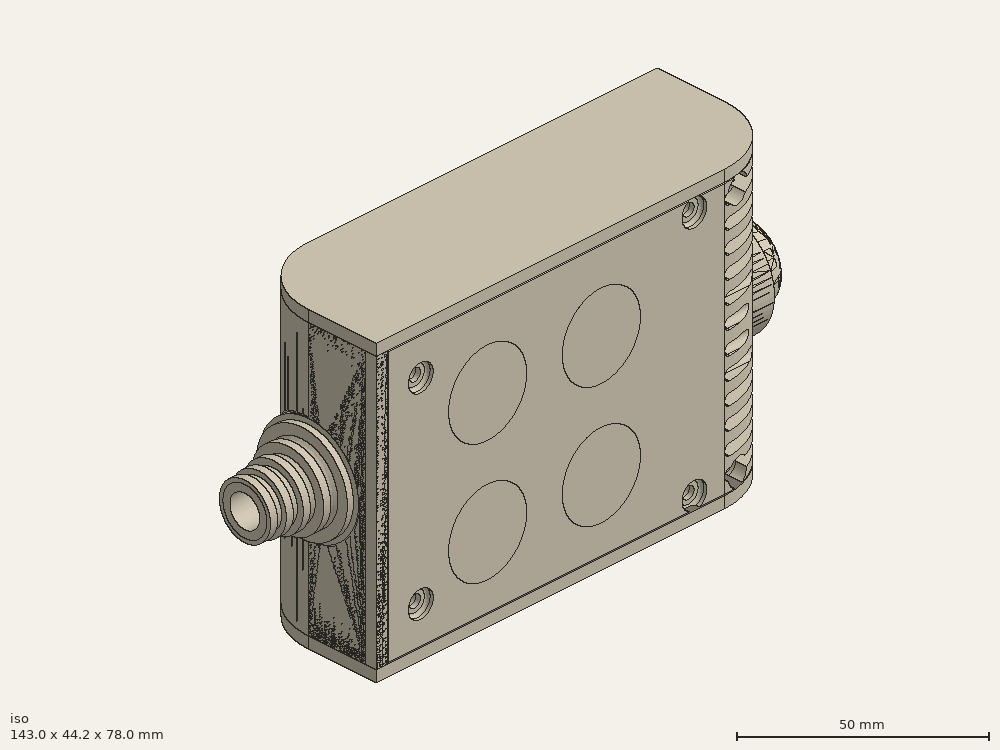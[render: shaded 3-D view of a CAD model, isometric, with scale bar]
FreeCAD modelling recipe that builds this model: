
FCSTD DOCUMENT  (FreeCAD 0.19R0.19.2)
Label: enclosure_124
License: All rights reserved
LicenseURL: http://en.wikipedia.org/wiki/All_rights_reserved
objects: Part::Feature×72, Part::Revolution×72, Part::MultiFuse×62, Sketcher::SketchObject×36, Part::Fillet×26, Part::Extrusion×25, Part::Cut×25, Part::Cylinder×22, Part::Box×12, App::MeasureDistance×4
note: 352 computed .brp shape members not serialized (recipe doc carries the construction recipe); baked Part::Feature solids carry a one-line shape summary decoded from their .brp

FEATURE [Sketcher::SketchObject] Sketch  label="topSketch"
  FullyConstrained = true
  sketch-geometry (13):
    g0: LineSegment StartX=117 StartY=19 StartZ=0 EndX=117 EndY=38 EndZ=0
    g1: ArcOfCircle CenterX=98 CenterY=19 CenterZ=0 NormalX=0 NormalY=0 NormalZ=1 AngleXU=0 Radius=19 StartAngle=5.7297 EndAngle=6.28319
    g2: LineSegment StartX=0 StartY=3 StartZ=0 EndX=0 EndY=19 EndZ=0
    g3: LineSegment StartX=19 StartY=38 StartZ=0 EndX=117 EndY=38 EndZ=0
    g4: ArcOfCircle CenterX=19 CenterY=19 CenterZ=0 NormalX=0 NormalY=0 NormalZ=1 AngleXU=0 Radius=19 StartAngle=1.5708 EndAngle=3.14159
    g5: ArcOfCircle CenterX=19 CenterY=19 CenterZ=0 NormalX=0 NormalY=0 NormalZ=1 AngleXU=0 Radius=16 StartAngle=1.5708 EndAngle=3.14159
    g6: ArcOfCircle CenterX=98 CenterY=19 CenterZ=0 NormalX=0 NormalY=0 NormalZ=1 AngleXU=0 Radius=16 StartAngle=5.60905 EndAngle=6.28319
    g7: LineSegment StartX=114 StartY=19 StartZ=0 EndX=114 EndY=35 EndZ=0
    g8: LineSegment StartX=110.5 StartY=9.01251 StartZ=0 EndX=114.163 EndY=9.01251 EndZ=0
    g9: LineSegment StartX=114 StartY=35 StartZ=0 EndX=19 EndY=35 EndZ=0
    g10: LineSegment StartX=0 StartY=3 StartZ=0 EndX=0 EndY=0 EndZ=0
    g11: LineSegment StartX=3 StartY=0 StartZ=0 EndX=0 EndY=0 EndZ=0
    g12: LineSegment StartX=3 StartY=19 StartZ=0 EndX=3 EndY=0 EndZ=0
  constraints (33):
    c: Vertical(g0)
    c: Distance(g0) = 19
    c: Block(g0)
    c: Coincident(g1,g0)
    c: Block(g1)
    c: Vertical(g2)
    c: Block(g2)
    c: Coincident(g3,g0)
    c: Horizontal(g3)
    c: Distance(g3) = 98
    c: Coincident(g4,g3)
    c: Coincident(g4,g2)
    c: Block(g4)
    c: Coincident(g5,g4)
    c: Coincident(g6,g1)
    c: Block(g6)
    c: Block(g5)
    c: Coincident(g7,g6)
    c: Vertical(g7)
    c: Coincident(g8,g6)
    c: Coincident(g8,g1)
    c: Coincident(g9,g7)
    c: Coincident(g9,g5)
    c: Horizontal(g9)
    c: Tangent(g9,g5)
    c: Coincident(g10,g2)
    c: Distance(g10) = 3
    c: Vertical(g10)
    c: Coincident(g11,g10)
    c: Horizontal(g11)
    c: Coincident(g12,g5)
    c: Coincident(g12,g11)
    c: Vertical(g12)
FEATURE [Sketcher::SketchObject] Sketch001  label="bottomSketch"
  FullyConstrained = true
  sketch-geometry (32):
    g0: LineSegment StartX=3.3 StartY=-6.03275e-07 StartZ=0 EndX=98 EndY=-6.03275e-07 EndZ=0
    g1: ArcOfCircle CenterX=98 CenterY=19 CenterZ=0 NormalX=0 NormalY=0 NormalZ=1 AngleXU=0 Radius=19 StartAngle=4.71239 EndAngle=5.71103
    g2: LineSegment StartX=6.3 StartY=8 StartZ=0 EndX=3.3 EndY=8 EndZ=0
    g3: LineSegment StartX=3.3 StartY=8 StartZ=0 EndX=3.3 EndY=-6.03275e-07 EndZ=0
    g4: ArcOfCircle CenterX=8.3 CenterY=5 CenterZ=0 NormalX=0 NormalY=0 NormalZ=1 AngleXU=0 Radius=2 StartAngle=3.14159 EndAngle=4.71239
    g5: LineSegment StartX=6.3 StartY=8 StartZ=0 EndX=6.3 EndY=5 EndZ=0
    g6: ArcOfCircle CenterX=98 CenterY=19 CenterZ=0 NormalX=0 NormalY=0 NormalZ=1 AngleXU=0 Radius=12.7 StartAngle=4.71239 EndAngle=6.28319
    g7: LineSegment StartX=94.7 StartY=3 StartZ=0 EndX=8.3 EndY=3 EndZ=0
    g8-g12: Circle x5 (B-spline internal-alignment scaffolding for g13; pole/knot coordinates omitted)
    g13: BSplineCurve PolesCount=5 KnotsCount=3 Degree=3 IsPeriodic=0
    g14: GeomPoint X=98 Y=6.3 Z=0
    g15: GeomPoint X=96.3938 Y=4.71946 Z=0
    g16: GeomPoint X=94.7 Y=3 Z=0
    g17-g23: Circle x7 (B-spline internal-alignment scaffolding for g24; pole/knot coordinates omitted)
    g24: BSplineCurve PolesCount=7 KnotsCount=5 Degree=3 IsPeriodic=0
    g25-g29: GeomPoint x5 (B-spline internal-alignment scaffolding for g24; pole/knot coordinates omitted)
    g30: ArcOfCircle CenterX=98 CenterY=19 CenterZ=0 NormalX=0 NormalY=0 NormalZ=1 AngleXU=0 Radius=15.7 StartAngle=5.81226 EndAngle=6.28319
    g31: LineSegment StartX=110.7 StartY=19 StartZ=0 EndX=113.7 EndY=19 EndZ=0
  constraints (41):
    c: Horizontal(g0)
    c: Coincident(g1,g0)
    c: Block(g1)
    c: Horizontal(g2)
    c: Distance(g2) = 3
    c: Coincident(g3,g2)
    c: Vertical(g3)
    c: Coincident(g3,g0)
    c: Block(g4)
    c: Block(g2)
    c: Coincident(g5,g2)
    c: Coincident(g5,g4)
    c: Vertical(g5)
    c: Coincident(g6,g1)
    c: Block(g6)
    c: Coincident(g7,g4)
    c: Horizontal(g7)
    c: Block(g0)
    c: Block(g7)
    c: Block(g3)
    c: Coincident(g13,g6)
    c: Weight(g8) = 1
    c: Equal(g8, g9-g12) x4
    c: Coincident(g13,g7)
    c: InternalAlignment(g8-g12 -> g13) x5
    c: InternalAlignment(g14,g13)
    c: InternalAlignment(g15,g13)
    c: InternalAlignment(g16,g13)
    c: Block(g13)
    c: Weight(g17) = 1
    c: Equal(g17, g18-g23) x6
    c: Coincident(g24,g1)
    c: InternalAlignment(g17-g23 -> g24) x7
    c: InternalAlignment(g25-g29 -> g24) x5
    c: Block(g24)
    c: Coincident(g30,g24)
    c: Coincident(g31,g6)
    c: Coincident(g31,g30)
    c: Horizontal(g31)
    c: Block(g31)
    c: Block(g30)
FEATURE [Part::Extrusion] Extrude  label="top"
  Base = -> Sketch
  Dir = (0,0,1)
  DirMode = 2
  FaceMakerClass = Part::FaceMakerBullseye
  LengthFwd = 72
  LengthRev = 0
  Solid = true
  Symmetric = false
FEATURE [Part::Extrusion] Extrude001  label="bottom"
  Base = -> Sketch001
  Dir = (0,0,1)
  DirMode = 2
  FaceMakerClass = Part::FaceMakerBullseye
  LengthFwd = 71.4
  LengthRev = 0
  Placement = pos=(0,0,0.3) rot=(0,0,1;0rad)
  Solid = true
  Symmetric = false
FEATURE [Sketcher::SketchObject] Sketch002  label="topSketch001"
  FullyConstrained = true
  sketch-geometry (6):
    g0: LineSegment StartX=19 StartY=38 StartZ=0 EndX=117 EndY=38 EndZ=0
    g1: ArcOfCircle CenterX=19 CenterY=19 CenterZ=0 NormalX=0 NormalY=0 NormalZ=1 AngleXU=0 Radius=19 StartAngle=1.5708 EndAngle=3.14159
    g2: LineSegment StartX=117 StartY=38 StartZ=0 EndX=117 EndY=19 EndZ=0
    g3: LineSegment StartX=98 StartY=1.0161e-12 StartZ=0 EndX=5.22862e-06 EndY=1.0161e-12 EndZ=0
    g4: LineSegment StartX=5.22862e-06 StartY=19 StartZ=0 EndX=5.22862e-06 EndY=1.0161e-12 EndZ=0
    g5: ArcOfCircle CenterX=98 CenterY=19 CenterZ=0 NormalX=0 NormalY=0 NormalZ=1 AngleXU=0 Radius=19 StartAngle=4.71239 EndAngle=6.28319
  constraints (16):
    c: Horizontal(g0)
    c: Distance(g0) = 98
    c: Coincident(g1,g0)
    c: Block(g1)
    c: Coincident(g2,g0)
    c: Vertical(g2)
    c: Distance(g2) = 19
    c: Horizontal(g3)
    c: Coincident(g4,g1)
    c: Vertical(g4)
    c: Coincident(g3,g4)
    c: Block(g3)
    c: Coincident(g5,g2)
    c: Coincident(g5,g3)
    c: Block(g0)
    c: Block(g5)
FEATURE [Part::Extrusion] Extrude002  label="sideA"
  Base = -> Sketch002
  Dir = (0,0,1)
  DirMode = 2
  FaceMakerClass = Part::FaceMakerBullseye
  LengthFwd = 3
  LengthRev = 0
  Placement = pos=(0,0,-3) rot=(0,0,1;0rad)
  Solid = true
  Symmetric = false
FEATURE [Sketcher::SketchObject] Sketch003  label="topSketch002"
  FullyConstrained = true
  sketch-geometry (6):
    g0: LineSegment StartX=19 StartY=38 StartZ=0 EndX=117 EndY=38 EndZ=0
    g1: ArcOfCircle CenterX=19 CenterY=19 CenterZ=0 NormalX=0 NormalY=0 NormalZ=1 AngleXU=0 Radius=19 StartAngle=1.5708 EndAngle=3.14159
    g2: LineSegment StartX=117 StartY=38 StartZ=0 EndX=117 EndY=19 EndZ=0
    g3: LineSegment StartX=98 StartY=1.0161e-12 StartZ=0 EndX=5.22862e-06 EndY=1.0161e-12 EndZ=0
    g4: LineSegment StartX=5.22862e-06 StartY=19 StartZ=0 EndX=5.22862e-06 EndY=1.0161e-12 EndZ=0
    g5: ArcOfCircle CenterX=98 CenterY=19 CenterZ=0 NormalX=0 NormalY=0 NormalZ=1 AngleXU=0 Radius=19 StartAngle=4.71239 EndAngle=6.28319
  constraints (16):
    c: Horizontal(g0)
    c: Distance(g0) = 98
    c: Coincident(g1,g0)
    c: Block(g1)
    c: Coincident(g2,g0)
    c: Vertical(g2)
    c: Distance(g2) = 19
    c: Horizontal(g3)
    c: Coincident(g4,g1)
    c: Vertical(g4)
    c: Coincident(g3,g4)
    c: Block(g3)
    c: Coincident(g5,g2)
    c: Coincident(g5,g3)
    c: Block(g0)
    c: Block(g5)
FEATURE [Part::Extrusion] Extrude003  label="sideB"
  Base = -> Sketch003
  Dir = (0,0,1)
  DirMode = 2
  FaceMakerClass = Part::FaceMakerBullseye
  LengthFwd = 3
  LengthRev = 0
  Placement = pos=(0,0,72) rot=(0,0,1;0rad)
  Solid = true
  Symmetric = false
FEATURE [Sketcher::SketchObject] Sketch004
  FullyConstrained = true
  MapMode = 3
  Placement = pos=(0,0,0) rot=(1,0,0;1.5708rad)
  Support = -> [Extrude]
  sketch-geometry (8):
    g0: Circle CenterX=80.351 CenterY=-67.6202 CenterZ=0 NormalX=0 NormalY=0 NormalZ=1 AngleXU=0 Radius=2
    g1: Circle CenterX=80.351 CenterY=-67.6202 CenterZ=0 NormalX=0 NormalY=0 NormalZ=1 AngleXU=0 Radius=3
    g2: Circle CenterX=80.351 CenterY=-4.92017 CenterZ=0 NormalX=0 NormalY=0 NormalZ=1 AngleXU=0 Radius=2
    g3: Circle CenterX=80.351 CenterY=-4.92017 CenterZ=0 NormalX=0 NormalY=0 NormalZ=1 AngleXU=0 Radius=3
    g4: Circle CenterX=23.851 CenterY=-4.92017 CenterZ=0 NormalX=0 NormalY=0 NormalZ=1 AngleXU=0 Radius=2
    g5: Circle CenterX=23.851 CenterY=-4.92017 CenterZ=0 NormalX=0 NormalY=0 NormalZ=1 AngleXU=0 Radius=3
    g6: Circle CenterX=23.851 CenterY=-67.6202 CenterZ=0 NormalX=0 NormalY=0 NormalZ=1 AngleXU=0 Radius=2
    g7: Circle CenterX=23.851 CenterY=-67.6202 CenterZ=0 NormalX=0 NormalY=0 NormalZ=1 AngleXU=0 Radius=3
  constraints (8):
    c: Block(g3)
    c: Block(g2)
    c: Block(g1)
    c: Block(g0)
    c: Block(g6)
    c: Block(g7)
    c: Block(g4)
    c: Block(g5)
FEATURE [Part::Extrusion] Extrude004
  Base = -> Sketch004
  Dir = (0,-1,2e-16)
  DirMode = 2
  FaceMakerClass = Part::FaceMakerBullseye
  LengthFwd = 6
  LengthRev = 0
  Placement = pos=(0,9,0) rot=(0,0,1;0rad)
  Solid = true
  Symmetric = false
FEATURE [Sketcher::SketchObject] Sketch005
  FullyConstrained = true
  MapMode = 3
  Placement = pos=(0,0,0) rot=(1,0,0;1.5708rad)
  Support = -> [Extrude]
  sketch-geometry (8):
    g0: Circle CenterX=80.351 CenterY=-67.6202 CenterZ=0 NormalX=0 NormalY=0 NormalZ=1 AngleXU=0 Radius=3
    g1: Circle CenterX=80.351 CenterY=-4.92017 CenterZ=0 NormalX=0 NormalY=0 NormalZ=1 AngleXU=0 Radius=3
    g2: Circle CenterX=23.851 CenterY=-4.92017 CenterZ=0 NormalX=0 NormalY=0 NormalZ=1 AngleXU=0 Radius=3
    g3: Circle CenterX=23.851 CenterY=-67.6202 CenterZ=0 NormalX=0 NormalY=0 NormalZ=1 AngleXU=0 Radius=3
    g4: Circle CenterX=23.851 CenterY=-67.6202 CenterZ=0 NormalX=0 NormalY=0 NormalZ=1 AngleXU=0 Radius=5
    g5: Circle CenterX=80.351 CenterY=-67.6202 CenterZ=0 NormalX=0 NormalY=0 NormalZ=1 AngleXU=0 Radius=5
    g6: Circle CenterX=23.851 CenterY=-4.92017 CenterZ=0 NormalX=0 NormalY=0 NormalZ=1 AngleXU=0 Radius=5
    g7: Circle CenterX=80.351 CenterY=-4.92017 CenterZ=0 NormalX=0 NormalY=0 NormalZ=1 AngleXU=0 Radius=5
  constraints (8):
    c: Block(g1)
    c: Block(g0)
    c: Block(g3)
    c: Block(g2)
    c: Block(g5)
    c: Block(g4)
    c: Block(g6)
    c: Block(g7)
FEATURE [Part::Extrusion] Extrude005
  Base = -> Sketch005
  Dir = (0,-1,2e-16)
  DirMode = 2
  FaceMakerClass = Part::FaceMakerBullseye
  LengthFwd = 2
  LengthRev = 0
  Solid = true
  Symmetric = false
FEATURE [Sketcher::SketchObject] Sketch006
  FullyConstrained = true
  MapMode = 3
  Placement = pos=(0,0,0) rot=(1,0,0;1.5708rad)
  sketch-geometry (8):
    g0: Circle CenterX=80.351 CenterY=-67.6202 CenterZ=0 NormalX=0 NormalY=0 NormalZ=1 AngleXU=0 Radius=3
    g1: Circle CenterX=80.351 CenterY=-4.92017 CenterZ=0 NormalX=0 NormalY=0 NormalZ=1 AngleXU=0 Radius=3
    g2: Circle CenterX=23.851 CenterY=-4.92017 CenterZ=0 NormalX=0 NormalY=0 NormalZ=1 AngleXU=0 Radius=3
    g3: Circle CenterX=23.851 CenterY=-67.6202 CenterZ=0 NormalX=0 NormalY=0 NormalZ=1 AngleXU=0 Radius=3
    g4: Circle CenterX=23.851 CenterY=-67.6202 CenterZ=0 NormalX=0 NormalY=0 NormalZ=1 AngleXU=0 Radius=5
    g5: Circle CenterX=80.351 CenterY=-67.6202 CenterZ=0 NormalX=0 NormalY=0 NormalZ=1 AngleXU=0 Radius=5
    g6: Circle CenterX=23.851 CenterY=-4.92017 CenterZ=0 NormalX=0 NormalY=0 NormalZ=1 AngleXU=0 Radius=5
    g7: Circle CenterX=80.351 CenterY=-4.92017 CenterZ=0 NormalX=0 NormalY=0 NormalZ=1 AngleXU=0 Radius=5
  constraints (8):
    c: Block(g1)
    c: Block(g0)
    c: Block(g3)
    c: Block(g2)
    c: Block(g5)
    c: Block(g4)
    c: Block(g6)
    c: Block(g7)
FEATURE [Part::Extrusion] Extrude007
  Base = -> Sketch006
  Dir = (0,-1,2e-16)
  DirMode = 2
  FaceMakerClass = Part::FaceMakerBullseye
  LengthFwd = 2
  LengthRev = 0
  Solid = true
  Symmetric = false
FEATURE [Part::Fillet] Fillet
  Base = -> Extrude007
  Edges = 4 edges r=1.99: [Edge6,Edge12,Edge18,Edge24]
FEATURE [Part::Cut] Cut
  Base = -> Extrude005
  Placement = pos=(0,5,0) rot=(0,0,1;0rad)
  Tool = -> Fillet
FEATURE [Part::MultiFuse] Fusion  label="pCBScrews"
  Placement = pos=(-2.5,0,72.3) rot=(0,0,1;0rad)
  Shapes = -> [Extrude004,Cut]
FEATURE [App::MeasureDistance] Distance  label="Distance: 0.69 mm"
  Distance = 0.685967
  P1 = (24.0138,2.9647,0.3)
  P2 = (23.8901,3,-0.373787)
FEATURE [App::MeasureDistance] Distance001  label="Distance: 0.53 mm"
  Distance = 0.533607
  P1 = (80.2939,3,72.2334)
  P2 = (80.281,2.99661,71.7)
FEATURE [Part::Fillet] Fillet001
  Base = -> Extrude001
  Edges = 1 edges r=2.4: [Edge17]
FEATURE [Part::Fillet] Fillet002  label="bottom001"
  Base = -> Fillet001
  Edges = 1 edges r=2.4: [Edge36]
FEATURE [Part::Fillet] Fillet003  label="top001"
  Base = -> Extrude
  Edges = 1 edges r=2: [Edge1]
FEATURE [Sketcher::SketchObject] Sketch007
  FullyConstrained = true
  sketch-geometry (16):
    g0: LineSegment StartX=4 StartY=0 StartZ=0 EndX=4 EndY=2.4 EndZ=0
    g1: LineSegment StartX=4 StartY=2.4 StartZ=0 EndX=7 EndY=2.4 EndZ=0
    g2: LineSegment StartX=4 StartY=0 StartZ=0 EndX=5.7 EndY=0 EndZ=0
    g3: LineSegment StartX=5.7 StartY=0 StartZ=0 EndX=5.7 EndY=-5.6 EndZ=0
    g4-g8: Circle x5 (B-spline internal-alignment scaffolding for g9; pole/knot coordinates omitted)
    g9: BSplineCurve PolesCount=5 KnotsCount=3 Degree=3 IsPeriodic=0
    g10: GeomPoint X=7 Y=2.4 Z=0
    g11: GeomPoint X=10.4582 Y=-1.55472 Z=0
    g12: GeomPoint X=14 Y=-5.6 Z=0
    g13: LineSegment StartX=14 StartY=-5.6 StartZ=0 EndX=14 EndY=-14.1 EndZ=0
    g14: LineSegment StartX=14 StartY=-14.1 StartZ=0 EndX=6.5 EndY=-14.1 EndZ=0
    g15: LineSegment StartX=5.7 StartY=-5.6 StartZ=0 EndX=6.5 EndY=-14.1 EndZ=0
  constraints (28):
    c: Distance(g0) = 2.4
    c: Vertical(g0)
    c: Block(g0)
    c: Coincident(g1,g0)
    c: Horizontal(g1)
    c: Distance(g1) = 3
    c: Coincident(g2,g0)
    c: Horizontal(g2)
    c: Distance(g2) = 1.7
    c: Coincident(g3,g2)
    c: Vertical(g3)
    c: Distance(g3) = 5.6
    c: Coincident(g9,g1)
    c: Weight(g4) = 1
    c: Equal(g4, g5-g8) x4
    c: InternalAlignment(g4-g8 -> g9) x5
    c: InternalAlignment(g10,g9)
    c: InternalAlignment(g11,g9)
    c: InternalAlignment(g12,g9)
    c: Block(g9)
    c: Coincident(g13,g9)
    c: Vertical(g13)
    c: Distance(g13) = 8.5
    c: Coincident(g14,g13)
    c: Horizontal(g14)
    c: Distance(g14) = 7.5
    c: Coincident(g15,g3)
    c: Coincident(g15,g14)
FEATURE [Part::Feature] Face
  shape: bbox 10 x 16.5 x 2e-07 mm, 1 faces, 0 solids (baked)
FEATURE [Part::Revolution] Revolve  label="plugHousing"
  Angle = 360
  Axis = (0,1,0)
  Base = (0,0,0)
  FaceMakerClass = Part::FaceMakerBullseye
  Placement = pos=(0,0,36.15) rot=(0,0,1;0rad)
  Solid = false
  Source = -> Face
  Symmetric = false
FEATURE [Part::Feature] Face001
  shape: bbox 10 x 16.5 x 2e-07 mm, 1 faces, 0 solids (baked)
FEATURE [Part::Revolution] Revolve001  label="plugHousing001"
  Angle = 360
  Axis = (0,1,0)
  Base = (0,0,0)
  FaceMakerClass = Part::FaceMakerBullseye
  Placement = pos=(0,0,36.15) rot=(0,0,1;0rad)
  Solid = false
  Source = -> Face001
  Symmetric = false
FEATURE [Part::MultiFuse] Fusion001  label="plugHousing002"
  Placement = pos=(0,0,0) rot=(0,0,1;1.5708rad)
  Shapes = -> [Revolve001,Revolve]
FEATURE [Part::Feature] Face002
  shape: bbox 10 x 16.5 x 2e-07 mm, 1 faces, 0 solids (baked)
FEATURE [Part::Revolution] Revolve003  label="plugHousing005"
  Angle = 360
  Axis = (0,1,0)
  Base = (0,0,0)
  FaceMakerClass = Part::FaceMakerBullseye
  Placement = pos=(0,0,36.15) rot=(0,0,1;0rad)
  Solid = false
  Source = -> Face002
  Symmetric = false
FEATURE [Part::Feature] Face003
  shape: bbox 10 x 16.5 x 2e-07 mm, 1 faces, 0 solids (baked)
FEATURE [Part::Revolution] Revolve002  label="plugHousing003"
  Angle = 360
  Axis = (0,1,0)
  Base = (0,0,0)
  FaceMakerClass = Part::FaceMakerBullseye
  Placement = pos=(0,0,36.15) rot=(0,0,1;0rad)
  Solid = false
  Source = -> Face003
  Symmetric = false
FEATURE [Part::MultiFuse] Fusion002  label="plugHousing004"
  Placement = pos=(0,0,0) rot=(0,0,1;1.5708rad)
  Shapes = -> [Revolve002,Revolve003]
FEATURE [Part::MultiFuse] Fusion003  label="plugHousing006"
  Placement = pos=(0,19,0) rot=(0,0,1;3.14159rad)
  Shapes = -> [Fusion002,Fusion001]
FEATURE [Part::Feature] Face004
  shape: bbox 10 x 16.5 x 2e-07 mm, 1 faces, 0 solids (baked)
FEATURE [Part::Revolution] Revolve006  label="plugHousing010"
  Angle = 360
  Axis = (0,1,0)
  Base = (0,0,0)
  FaceMakerClass = Part::FaceMakerBullseye
  Placement = pos=(0,0,36.15) rot=(0,0,1;0rad)
  Solid = false
  Source = -> Face004
  Symmetric = false
FEATURE [Part::Feature] Face005
  shape: bbox 10 x 16.5 x 2e-07 mm, 1 faces, 0 solids (baked)
FEATURE [Part::Revolution] Revolve007  label="plugHousing011"
  Angle = 360
  Axis = (0,1,0)
  Base = (0,0,0)
  FaceMakerClass = Part::FaceMakerBullseye
  Placement = pos=(0,0,36.15) rot=(0,0,1;0rad)
  Solid = false
  Source = -> Face005
  Symmetric = false
FEATURE [Part::Feature] Face006
  shape: bbox 10 x 16.5 x 2e-07 mm, 1 faces, 0 solids (baked)
FEATURE [Part::Revolution] Revolve004  label="plugHousing007"
  Angle = 360
  Axis = (0,1,0)
  Base = (0,0,0)
  FaceMakerClass = Part::FaceMakerBullseye
  Placement = pos=(0,0,36.15) rot=(0,0,1;0rad)
  Solid = false
  Source = -> Face006
  Symmetric = false
FEATURE [Part::MultiFuse] Fusion004  label="plugHousing009"
  Placement = pos=(0,0,0) rot=(0,0,1;1.5708rad)
  Shapes = -> [Revolve004,Revolve007]
FEATURE [Part::Feature] Face007
  shape: bbox 10 x 16.5 x 2e-07 mm, 1 faces, 0 solids (baked)
FEATURE [Part::Revolution] Revolve005  label="plugHousing008"
  Angle = 360
  Axis = (0,1,0)
  Base = (0,0,0)
  FaceMakerClass = Part::FaceMakerBullseye
  Placement = pos=(0,0,36.15) rot=(0,0,1;0rad)
  Solid = false
  Source = -> Face007
  Symmetric = false
FEATURE [Part::MultiFuse] Fusion005  label="plugHousing012"
  Placement = pos=(0,0,0) rot=(0,0,1;1.5708rad)
  Shapes = -> [Revolve006,Revolve005]
FEATURE [Part::MultiFuse] Fusion006  label="plugHousing013"
  Placement = pos=(0,19,0) rot=(0,0,1;3.14159rad)
  Shapes = -> [Fusion005,Fusion004]
FEATURE [Part::MultiFuse] Fusion007  label="plugHousing014"
  Placement = pos=(122.621,0,-0.15) rot=(0,0,1;0rad)
  Shapes = -> [Fusion003,Fusion006]
FEATURE [Part::Cylinder] Cylinder002
  Angle = 360
  AttacherType = Attacher::AttachEngine3D
  Height = 20
  Placement = pos=(0,0,36.15) rot=(0,0,1;0rad)
  Radius = 4
FEATURE [Part::Cylinder] Cylinder003
  Angle = 360
  AttacherType = Attacher::AttachEngine3D
  Height = 10
  Placement = pos=(0,0,36.15) rot=(0,0,1;0rad)
  Radius = 4
FEATURE [Part::MultiFuse] Fusion009  label="removeToCreateHoleForPlugHousing"
  Placement = pos=(70,19,36.15) rot=(0,1,0;1.5708rad)
  Shapes = -> [Cylinder002,Cylinder003]
FEATURE [Part::Cylinder] Cylinder004
  Angle = 360
  AttacherType = Attacher::AttachEngine3D
  Height = 20
  Placement = pos=(0,0,36.15) rot=(0,0,1;0rad)
  Radius = 4
FEATURE [Part::Cylinder] Cylinder005
  Angle = 360
  AttacherType = Attacher::AttachEngine3D
  Height = 10
  Placement = pos=(0,0,36.15) rot=(0,0,1;0rad)
  Radius = 4
FEATURE [Part::MultiFuse] Fusion010  label="removeToCreateHoleForPlugHousing001"
  Placement = pos=(70,19,36.15) rot=(0,1,0;1.5708rad)
  Shapes = -> [Cylinder004,Cylinder005]
FEATURE [Part::Cut] Cut001
  Base = -> Fillet003
  Tool = -> Fusion010
FEATURE [Part::Cut] Cut002  label="Bottom"
  Base = -> Fillet002
  Tool = -> Fusion009
FEATURE [Part::Feature] Face008
  shape: bbox 10 x 16.5 x 2e-07 mm, 1 faces, 0 solids (baked)
FEATURE [Part::Revolution] Revolve011  label="plugHousing021"
  Angle = 360
  Axis = (0,1,0)
  Base = (0,0,0)
  FaceMakerClass = Part::FaceMakerBullseye
  Placement = pos=(0,0,36.15) rot=(0,0,1;0rad)
  Solid = false
  Source = -> Face008
  Symmetric = false
FEATURE [Part::Feature] Face009
  shape: bbox 10 x 16.5 x 2e-07 mm, 1 faces, 0 solids (baked)
FEATURE [Part::Revolution] Revolve012  label="plugHousing022"
  Angle = 360
  Axis = (0,1,0)
  Base = (0,0,0)
  FaceMakerClass = Part::FaceMakerBullseye
  Placement = pos=(0,0,36.15) rot=(0,0,1;0rad)
  Solid = false
  Source = -> Face009
  Symmetric = false
FEATURE [Part::Feature] Face010 .. Face013  x4 (patterned run collapsed; names and placements below)
  shape: bbox 10 x 16.5 x 2e-07 mm, 1 faces, 0 solids (baked)
FEATURE [Part::Revolution] Revolve015  label="plugHousing027"
  Angle = 360
  Axis = (0,1,0)
  Base = (0,0,0)
  FaceMakerClass = Part::FaceMakerBullseye
  Placement = pos=(0,0,36.15) rot=(0,0,1;0rad)
  Solid = false
  Source = -> Face013
  Symmetric = false
FEATURE [Part::Feature] Face014
  shape: bbox 10 x 16.5 x 2e-07 mm, 1 faces, 0 solids (baked)
FEATURE [Part::Feature] Face015
  shape: bbox 10 x 16.5 x 2e-07 mm, 1 faces, 0 solids (baked)
FEATURE [Part::Feature] Face016
  shape: bbox 10 x 16.5 x 2e-07 mm, 1 faces, 0 solids (baked)
FEATURE [Part::Revolution] Revolve019  label="plugHousing033"
  Angle = 360
  Axis = (0,1,0)
  Base = (0,0,0)
  FaceMakerClass = Part::FaceMakerBullseye
  Placement = pos=(0,0,36.15) rot=(0,0,1;0rad)
  Solid = false
  Source = -> Face016
  Symmetric = false
FEATURE [Part::Feature] Face017
  shape: bbox 10 x 16.5 x 2e-07 mm, 1 faces, 0 solids (baked)
FEATURE [Part::Revolution] Revolve020  label="plugHousing034"
  Angle = 360
  Axis = (0,1,0)
  Base = (0,0,0)
  FaceMakerClass = Part::FaceMakerBullseye
  Placement = pos=(0,0,36.15) rot=(0,0,1;0rad)
  Solid = false
  Source = -> Face017
  Symmetric = false
FEATURE [Part::Feature] Face018
  shape: bbox 10 x 16.5 x 2e-07 mm, 1 faces, 0 solids (baked)
FEATURE [Part::Revolution] Revolve016  label="plugHousing030"
  Angle = 360
  Axis = (0,1,0)
  Base = (0,0,0)
  FaceMakerClass = Part::FaceMakerBullseye
  Placement = pos=(0,0,36.15) rot=(0,0,1;0rad)
  Solid = false
  Source = -> Face018
  Symmetric = false
FEATURE [Part::MultiFuse] Fusion020  label="plugHousing038"
  Placement = pos=(0,0,0) rot=(0,0,1;1.5708rad)
  Shapes = -> [Revolve016,Revolve020]
FEATURE [Part::Feature] Face019
  shape: bbox 10 x 16.5 x 2e-07 mm, 1 faces, 0 solids (baked)
FEATURE [Part::Feature] Face020
  shape: bbox 10 x 16.5 x 2e-07 mm, 1 faces, 0 solids (baked)
FEATURE [Part::Revolution] Revolve017  label="plugHousing031"
  Angle = 360
  Axis = (0,1,0)
  Base = (0,0,0)
  FaceMakerClass = Part::FaceMakerBullseye
  Placement = pos=(0,0,36.15) rot=(0,0,1;0rad)
  Solid = false
  Source = -> Face020
  Symmetric = false
FEATURE [Part::MultiFuse] Fusion021  label="plugHousing039"
  Placement = pos=(0,0,0) rot=(0,0,1;1.5708rad)
  Shapes = -> [Revolve019,Revolve017]
FEATURE [Part::MultiFuse] Fusion023  label="plugHousing041"
  Placement = pos=(0,19,0) rot=(0,0,1;3.14159rad)
  Shapes = -> [Fusion021,Fusion020]
FEATURE [Part::Revolution] Revolve022  label="plugHousing043"
  Angle = 360
  Axis = (0,1,0)
  Base = (0,0,0)
  FaceMakerClass = Part::FaceMakerBullseye
  Placement = pos=(0,0,36.15) rot=(0,0,1;0rad)
  Solid = false
  Source = -> Face019
  Symmetric = false
FEATURE [Part::Feature] Face021
  shape: bbox 10 x 16.5 x 2e-07 mm, 1 faces, 0 solids (baked)
FEATURE [Part::Revolution] Revolve023  label="plugHousing044"
  Angle = 360
  Axis = (0,1,0)
  Base = (0,0,0)
  FaceMakerClass = Part::FaceMakerBullseye
  Placement = pos=(0,0,36.15) rot=(0,0,1;0rad)
  Solid = false
  Source = -> Face021
  Symmetric = false
FEATURE [Part::Feature] Face022
  shape: bbox 10 x 16.5 x 2e-07 mm, 1 faces, 0 solids (baked)
FEATURE [Part::Revolution] Revolve018  label="plugHousing032"
  Angle = 360
  Axis = (0,1,0)
  Base = (0,0,0)
  FaceMakerClass = Part::FaceMakerBullseye
  Placement = pos=(0,0,36.15) rot=(0,0,1;0rad)
  Solid = false
  Source = -> Face022
  Symmetric = false
FEATURE [Part::MultiFuse] Fusion022  label="plugHousing040"
  Placement = pos=(0,0,0) rot=(0,0,1;1.5708rad)
  Shapes = -> [Revolve018,Revolve023]
FEATURE [Part::Feature] Face023
  shape: bbox 10 x 16.5 x 2e-07 mm, 1 faces, 0 solids (baked)
FEATURE [Part::Revolution] Revolve021  label="plugHousing035"
  Angle = 360
  Axis = (0,1,0)
  Base = (0,0,0)
  FaceMakerClass = Part::FaceMakerBullseye
  Placement = pos=(0,0,36.15) rot=(0,0,1;0rad)
  Solid = false
  Source = -> Face023
  Symmetric = false
FEATURE [Part::MultiFuse] Fusion018  label="plugHousing036"
  Placement = pos=(0,0,0) rot=(0,0,1;1.5708rad)
  Shapes = -> [Revolve022,Revolve021]
FEATURE [Part::MultiFuse] Fusion019  label="plugHousing037"
  Placement = pos=(0,19,0) rot=(0,0,1;3.14159rad)
  Shapes = -> [Fusion018,Fusion022]
FEATURE [Part::MultiFuse] Fusion024  label="plugHousing042"
  Placement = pos=(122.621,0,-0.15) rot=(0,0,1;0rad)
  Shapes = -> [Fusion023,Fusion019]
FEATURE [Part::Cylinder] Cylinder006
  Angle = 360
  AttacherType = Attacher::AttachEngine3D
  Height = 20
  Placement = pos=(0,0,36.15) rot=(0,0,1;0rad)
  Radius = 14.3
FEATURE [Part::Cylinder] Cylinder007
  Angle = 360
  AttacherType = Attacher::AttachEngine3D
  Height = 10
  Placement = pos=(0,0,36.15) rot=(0,0,1;0rad)
  Radius = 4
FEATURE [Part::MultiFuse] Fusion026  label="removeToCreteHoleForPlugHousing"
  Placement = pos=(70,19,36) rot=(0,1,0;1.5708rad)
  Shapes = -> [Cylinder006,Cylinder007]
FEATURE [Part::Box] Box001  label="Cube001"
  AttacherType = Attacher::AttachEngine3D
  Height = 28
  Length = 3
  Placement = pos=(110.7,19,22) rot=(0,0,1;0rad)
  Width = 15.7
FEATURE [Part::Cut] Cut003  label="top002"
  Base = -> Cut001
  Tool = -> Fusion007
FEATURE [Part::Revolution] Revolve008  label="plugHousing015"
  Angle = 360
  Axis = (0,1,0)
  Base = (0,0,0)
  FaceMakerClass = Part::FaceMakerBullseye
  Placement = pos=(0,0,36.15) rot=(0,0,1;0rad)
  Solid = false
  Source = -> Face010
  Symmetric = false
FEATURE [Part::MultiFuse] Fusion013  label="plugHousing020"
  Placement = pos=(0,0,0) rot=(0,0,1;1.5708rad)
  Shapes = -> [Revolve008,Revolve012]
FEATURE [Part::Cut] Cut004  label="top003"
  Base = -> Cut003
  Placement = pos=(1,0,0) rot=(0,0,1;0rad)
  Tool = -> Fusion026
FEATURE [Part::Cylinder] Cylinder008
  Angle = 360
  AttacherType = Attacher::AttachEngine3D
  Height = 20
  Placement = pos=(0,0,36.15) rot=(0,0,1;0rad)
  Radius = 10.3
FEATURE [Part::Cylinder] Cylinder009
  Angle = 360
  AttacherType = Attacher::AttachEngine3D
  Height = 10
  Placement = pos=(0,0,36.15) rot=(0,0,1;0rad)
  Radius = 4
FEATURE [Part::MultiFuse] Fusion027  label="removeToCreteHoleForPlugHousing001"
  Placement = pos=(70,19,36) rot=(0,1,0;1.5708rad)
  Shapes = -> [Cylinder008,Cylinder009]
FEATURE [Part::Cut] Cut005  label="plugHousingTab"
  Base = -> Box001
  Tool = -> Fusion027
FEATURE [Part::MultiFuse] Fusion028  label="plugHousing045"
  Shapes = -> [Fusion024,Cut005]
FEATURE [Part::Box] Box002  label="Cube002"
  AttacherType = Attacher::AttachEngine3D
  Height = 28.8
  Length = 3
  Placement = pos=(107.3,28,21.6) rot=(0,0,1;0rad)
  Width = 7
FEATURE [Part::Box] Box003  label="Cube003"
  AttacherType = Attacher::AttachEngine3D
  Height = 3
  Length = 6.4
  Placement = pos=(107.3,28,18.6) rot=(0,0,1;0rad)
  Width = 7
FEATURE [Part::Box] Box004  label="Cube004"
  AttacherType = Attacher::AttachEngine3D
  Height = 3
  Length = 6.4
  Placement = pos=(107.3,28,50.4) rot=(0,0,1;0rad)
  Width = 7
FEATURE [Part::MultiFuse] Fusion029  label="plugHousingBracketHolder"
  Shapes = -> [Box004,Box002,Box003]
FEATURE [Part::Cylinder] Cylinder010
  Angle = 360
  AttacherType = Attacher::AttachEngine3D
  Height = 20
  Placement = pos=(0,0,36.15) rot=(0,0,1;0rad)
  Radius = 14.3
FEATURE [Part::Cylinder] Cylinder011
  Angle = 360
  AttacherType = Attacher::AttachEngine3D
  Height = 10
  Placement = pos=(0,0,36.15) rot=(0,0,1;0rad)
  Radius = 4
FEATURE [Part::MultiFuse] Fusion030  label="removeToCreteHoleForPlugHousing002"
  Placement = pos=(70,19,36) rot=(0,1,0;1.5708rad)
  Shapes = -> [Cylinder010,Cylinder011]
FEATURE [Part::Cut] Cut006  label="plugHousingBracketHolder001"
  Base = -> Fusion029
  Tool = -> Fusion030
FEATURE [Part::Cylinder] Cylinder012
  Angle = 360
  AttacherType = Attacher::AttachEngine3D
  Height = 20
  Placement = pos=(0,0,36.15) rot=(0,0,1;0rad)
  Radius = 7
FEATURE [Part::Cylinder] Cylinder013
  Angle = 360
  AttacherType = Attacher::AttachEngine3D
  Height = 10
  Placement = pos=(0,0,36.15) rot=(0,0,1;0rad)
  Radius = 4
FEATURE [Part::MultiFuse] Fusion032  label="removeToCreteHoleForPlugHousing003"
  Placement = pos=(70,19,36) rot=(0,1,0;1.5708rad)
  Shapes = -> [Cylinder012,Cylinder013]
FEATURE [Part::Cut] Cut007  label="bottom002"
  Base = -> Cut002
  Tool = -> Fusion032
FEATURE [Sketcher::SketchObject] Sketch008
  FullyConstrained = true
  sketch-geometry (54):
    g0: LineSegment StartX=-4.2 StartY=0 StartZ=0 EndX=-6.2 EndY=0 EndZ=0
    g1: LineSegment StartX=-14 StartY=-18 StartZ=0 EndX=-14 EndY=-26.5 EndZ=0
    g2: LineSegment StartX=-4.2 StartY=0 StartZ=0 EndX=-4.2 EndY=-13.4877 EndZ=0
    g3: Circle CenterX=-4.2 CenterY=-13.4877 CenterZ=0 NormalX=0 NormalY=0 NormalZ=1 AngleXU=0 Radius=1
    g4: Circle CenterX=-4.2 CenterY=-26.5 CenterZ=0 NormalX=0 NormalY=0 NormalZ=1 AngleXU=0 Radius=1
    g5: Circle CenterX=-8.2 CenterY=-26.5 CenterZ=0 NormalX=0 NormalY=0 NormalZ=1 AngleXU=0 Radius=1
    g6: BSplineCurve PolesCount=3 KnotsCount=2 Degree=2 IsPeriodic=0
    g7: GeomPoint X=-4.2 Y=-13.4877 Z=0
    g8: GeomPoint X=-8.2 Y=-26.5 Z=0
    g9: LineSegment StartX=-14 StartY=-26.5 StartZ=0 EndX=-8.2 EndY=-26.5 EndZ=0
    g10: LineSegment StartX=-10.15 StartY=-12 StartZ=0 EndX=-10.15 EndY=-14 EndZ=0
    g11: LineSegment StartX=-12.8401 StartY=-16 StartZ=0 EndX=-10.1571 EndY=-16 EndZ=0
    g12: LineSegment StartX=-10.15 StartY=-14 StartZ=0 EndX=-8.70761 EndY=-14 EndZ=0
    g13: LineSegment StartX=-12.8401 StartY=-16 StartZ=0 EndX=-12.8401 EndY=-17.6958 EndZ=0
    g14: LineSegment StartX=-10.15 StartY=-12 StartZ=0 EndX=-7.79258 EndY=-12 EndZ=0
    g15: Circle CenterX=-6.2215 CenterY=-2 CenterZ=0 NormalX=0 NormalY=0 NormalZ=1 AngleXU=0 Radius=1
    g16: Circle CenterX=-6.22762 CenterY=-2.58724 CenterZ=0 NormalX=0 NormalY=0 NormalZ=1 AngleXU=0 Radius=1
    g17: Circle CenterX=-6.32538 CenterY=-4 CenterZ=0 NormalX=0 NormalY=0 NormalZ=1 AngleXU=0 Radius=1
    g18: BSplineCurve PolesCount=3 KnotsCount=2 Degree=2 IsPeriodic=0
    g19: GeomPoint X=-6.2215 Y=-2 Z=0
    g20: GeomPoint X=-6.32538 Y=-4 Z=0
    g21: Circle CenterX=-6.48644 CenterY=-5.99526 CenterZ=0 NormalX=0 NormalY=0 NormalZ=1 AngleXU=0 Radius=1
    g22: Circle CenterX=-6.58486 CenterY=-6.99526 CenterZ=0 NormalX=0 NormalY=0 NormalZ=1 AngleXU=0 Radius=1
    g23: Circle CenterX=-6.77343 CenterY=-8 CenterZ=0 NormalX=0 NormalY=0 NormalZ=1 AngleXU=0 Radius=1
    g24: BSplineCurve PolesCount=3 KnotsCount=2 Degree=2 IsPeriodic=0
    g25: GeomPoint X=-6.48644 Y=-5.99526 Z=0
    g26: GeomPoint X=-6.77343 Y=-8 Z=0
    g27: Circle CenterX=-7.19003 CenterY=-10 CenterZ=0 NormalX=0 NormalY=0 NormalZ=1 AngleXU=0 Radius=1
    g28: Circle CenterX=-7.44407 CenterY=-11.0915 CenterZ=0 NormalX=0 NormalY=0 NormalZ=1 AngleXU=0 Radius=1
    g29: Circle CenterX=-7.79258 CenterY=-12 CenterZ=0 NormalX=0 NormalY=0 NormalZ=1 AngleXU=0 Radius=1
    g30: BSplineCurve PolesCount=3 KnotsCount=2 Degree=2 IsPeriodic=0
    g31: GeomPoint X=-7.19003 Y=-10 Z=0
    g32: GeomPoint X=-7.79258 Y=-12 Z=0
    g33: Circle CenterX=-8.70761 CenterY=-14 CenterZ=0 NormalX=0 NormalY=0 NormalZ=1 AngleXU=0 Radius=1
    g34: Circle CenterX=-9.33087 CenterY=-15.1837 CenterZ=0 NormalX=0 NormalY=0 NormalZ=1 AngleXU=0 Radius=1
    g35: Circle CenterX=-10.1571 CenterY=-16 CenterZ=0 NormalX=0 NormalY=0 NormalZ=1 AngleXU=0 Radius=1
    g36: BSplineCurve PolesCount=3 KnotsCount=2 Degree=2 IsPeriodic=0
    g37: GeomPoint X=-8.70761 Y=-14 Z=0
    g38: GeomPoint X=-10.1571 Y=-16 Z=0
    g39: Circle CenterX=-12.8401 CenterY=-17.6958 CenterZ=0 NormalX=0 NormalY=0 NormalZ=1 AngleXU=0 Radius=1
    g40: Circle CenterX=-13.3521 CenterY=-17.9027 CenterZ=0 NormalX=0 NormalY=0 NormalZ=1 AngleXU=0 Radius=1
    g41: Circle CenterX=-14 CenterY=-18 CenterZ=0 NormalX=0 NormalY=0 NormalZ=1 AngleXU=0 Radius=1
    g42: BSplineCurve PolesCount=3 KnotsCount=2 Degree=2 IsPeriodic=0
    g43: GeomPoint X=-12.8401 Y=-17.6958 Z=0
    g44: GeomPoint X=-14 Y=-18 Z=0
    g45: LineSegment StartX=-6.2 StartY=0 StartZ=0 EndX=-7.2 EndY=0 EndZ=0
    g46: LineSegment StartX=-7.2 StartY=0 StartZ=0 EndX=-7.2 EndY=-2 EndZ=0
    g47: LineSegment StartX=-7.2 StartY=-2 StartZ=0 EndX=-6.2215 EndY=-2 EndZ=0
    g48: LineSegment StartX=-6.32538 StartY=-4 StartZ=0 EndX=-7.65538 EndY=-4 EndZ=0
    g49: LineSegment StartX=-7.65538 StartY=-4 StartZ=0 EndX=-7.65538 EndY=-5.99526 EndZ=0
    g50: LineSegment StartX=-7.65538 StartY=-5.99526 StartZ=0 EndX=-6.48644 EndY=-5.99526 EndZ=0
    g51: LineSegment StartX=-6.77343 StartY=-8 StartZ=0 EndX=-8.43343 EndY=-8 EndZ=0
    g52: LineSegment StartX=-8.43343 StartY=-8 StartZ=0 EndX=-8.43343 EndY=-10 EndZ=0
    g53: LineSegment StartX=-8.43343 StartY=-10 StartZ=0 EndX=-7.19003 EndY=-10 EndZ=0
  constraints (112):
    c: Horizontal(g0)
    c: Distance(g0) = 2
    c: Block(g0)
    c: Vertical(g1)
    c: Coincident(g2,g0)
    c: Vertical(g2)
    c: Block(g2)
    c: Coincident(g6,g2)
    c: Weight(g3) = 1
    c: Equal(g3,g4)
    c: Equal(g3,g5)
    c: InternalAlignment(g3,g6)
    c: InternalAlignment(g4,g6)
    c: InternalAlignment(g5,g6)
    c: InternalAlignment(g7,g6)
    c: InternalAlignment(g8,g6)
    c: Block(g6)
    c: Coincident(g9,g1)
    c: Coincident(g9,g6)
    c: Horizontal(g9)
    c: Vertical(g10)
    c: Block(g10)
    c: Horizontal(g11)
    c: Block(g11)
    c: Coincident(g12,g10)
    c: Horizontal(g12)
    c: Block(g12)
    c: Coincident(g13,g11)
    c: Vertical(g13)
    c: Block(g13)
    c: Coincident(g14,g10)
    c: Horizontal(g14)
    c: Block(g14)
    c: Block(g9)
    c: Block(g1)
    c: Weight(g15) = 1
    c: Equal(g15,g16)
    c: Equal(g15,g17)
    c: InternalAlignment(g15,g18)
    c: InternalAlignment(g16,g18)
    c: InternalAlignment(g17,g18)
    c: InternalAlignment(g19,g18)
    c: InternalAlignment(g20,g18)
    c: Weight(g21) = 1
    c: Equal(g21,g22)
    c: Equal(g21,g23)
    c: InternalAlignment(g21,g24)
    c: InternalAlignment(g22,g24)
    c: InternalAlignment(g23,g24)
    c: InternalAlignment(g25,g24)
    c: InternalAlignment(g26,g24)
    c: Weight(g27) = 1
    c: Equal(g27,g28)
    c: Equal(g27,g29)
    c: Coincident(g30,g14)
    c: InternalAlignment(g27,g30)
    c: InternalAlignment(g28,g30)
    c: InternalAlignment(g29,g30)
    c: InternalAlignment(g31,g30)
    c: InternalAlignment(g32,g30)
    c: Coincident(g36,g12)
    c: Weight(g33) = 1
    c: Equal(g33,g34)
    c: Equal(g33,g35)
    c: Coincident(g36,g11)
    c: InternalAlignment(g33,g36)
    c: InternalAlignment(g34,g36)
    c: InternalAlignment(g35,g36)
    c: InternalAlignment(g37,g36)
    c: InternalAlignment(g38,g36)
    c: Coincident(g42,g13)
    c: Weight(g39) = 1
    c: Equal(g39,g40)
    c: Equal(g39,g41)
    c: Coincident(g42,g1)
    c: InternalAlignment(g39,g42)
    c: InternalAlignment(g40,g42)
    c: InternalAlignment(g41,g42)
    c: InternalAlignment(g43,g42)
    c: InternalAlignment(g44,g42)
    c: Block(g18)
    c: Block(g24)
    c: Block(g30)
    c: Block(g36)
    c: Block(g42)
    c: Horizontal(g45)
    c: Coincident(g45,g0)
    c: Vertical(g46)
    c: Coincident(g46,g45)
    c: Coincident(g47,g46)
    c: Coincident(g47,g18)
    c: Horizontal(g47)
    c: Block(g46)
    c: Coincident(g48,g18)
    c: Horizontal(g48)
    c: Distance(g48) = 1.33
    c: Vertical(g49)
    c: Coincident(g49,g48)
    c: Coincident(g50,g49)
    c: Coincident(g50,g24)
    c: Horizontal(g50)
    c: Tangent(g50,g22)
    c: Horizontal(g51)
    c: Coincident(g51,g24)
    c: Block(g51)
    c: Vertical(g52)
    c: Block(g52)
    c: Coincident(g52,g51)
    c: Coincident(g53,g52)
    c: Coincident(g53,g30)
    c: Horizontal(g53)
    c: Distance(g1) = 8.5
FEATURE [Part::Feature] Face024
  shape: bbox 9.8 x 26.5 x 2e-07 mm, 1 faces, 0 solids (baked)
FEATURE [Part::Revolution] Revolve024
  Angle = 360
  Axis = (0,1,0)
  Base = (0,0,0)
  FaceMakerClass = Part::FaceMakerBullseye
  Placement = pos=(0,0,0) rot=(0,0,1;1.5708rad)
  Solid = false
  Source = -> Face024
  Symmetric = false
FEATURE [Part::Feature] Face025
  shape: bbox 9.8 x 26.5 x 2e-07 mm, 1 faces, 0 solids (baked)
FEATURE [Part::Revolution] Revolve025
  Angle = 360
  Axis = (0,1,0)
  Base = (0,0,0)
  FaceMakerClass = Part::FaceMakerBullseye
  Placement = pos=(0,0,0) rot=(0,0,1;1.5708rad)
  Solid = false
  Source = -> Face025
  Symmetric = false
FEATURE [Part::MultiFuse] Fusion033
  Placement = pos=(-18,19,36) rot=(0,0,1;0rad)
  Shapes = -> [Revolve025,Revolve024]
FEATURE [Part::Cylinder] Cylinder014
  Angle = 360
  AttacherType = Attacher::AttachEngine3D
  Height = 20
  Placement = pos=(0,0,36.15) rot=(0,0,1;0rad)
  Radius = 14.3
FEATURE [Part::Cylinder] Cylinder015
  Angle = 360
  AttacherType = Attacher::AttachEngine3D
  Height = 10
  Placement = pos=(0,0,36.15) rot=(0,0,1;0rad)
  Radius = 4
FEATURE [Part::MultiFuse] Fusion034  label="removeToCreteHoleForPlugHousing004"
  Placement = pos=(-42,19,36) rot=(0,1,0;1.5708rad)
  Shapes = -> [Cylinder014,Cylinder015]
FEATURE [Part::Cut] Cut008  label="top004"
  Base = -> Cut004
  Placement = pos=(-1,0,0) rot=(0,0,1;0rad)
  Tool = -> Fusion034
FEATURE [Part::Box] Box005  label="Cube005"
  AttacherType = Attacher::AttachEngine3D
  Height = 28
  Length = 3
  Placement = pos=(110.7,19,22) rot=(0,0,1;0rad)
  Width = 15.7
FEATURE [Part::Cylinder] Cylinder016
  Angle = 360
  AttacherType = Attacher::AttachEngine3D
  Height = 10
  Placement = pos=(0,0,36.15) rot=(0,0,1;0rad)
  Radius = 4
FEATURE [Part::Cylinder] Cylinder017
  Angle = 360
  AttacherType = Attacher::AttachEngine3D
  Height = 20
  Placement = pos=(0,0,36.15) rot=(0,0,1;0rad)
  Radius = 10.3
FEATURE [Part::MultiFuse] Fusion035  label="removeToCreteHoleForPlugHousing005"
  Placement = pos=(70,19,36) rot=(0,1,0;1.5708rad)
  Shapes = -> [Cylinder017,Cylinder016]
FEATURE [Part::Cut] Cut009  label="plugHousingTab001"
  Base = -> Box005
  Placement = pos=(-107.4,-14,0) rot=(0,0,1;0rad)
  Tool = -> Fusion035
FEATURE [Part::Box] Box006  label="Cube006"
  AttacherType = Attacher::AttachEngine3D
  Height = 28
  Length = 3
  Placement = pos=(110.7,19,22) rot=(0,0,1;0rad)
  Width = 15.7
FEATURE [Part::Cylinder] Cylinder018
  Angle = 360
  AttacherType = Attacher::AttachEngine3D
  Height = 10
  Placement = pos=(0,0,36.15) rot=(0,0,1;0rad)
  Radius = 4
FEATURE [Part::Cylinder] Cylinder019
  Angle = 360
  AttacherType = Attacher::AttachEngine3D
  Height = 20
  Placement = pos=(0,0,36.15) rot=(0,0,1;0rad)
  Radius = 10.3
FEATURE [Part::MultiFuse] Fusion036  label="removeToCreteHoleForPlugHousing006"
  Placement = pos=(70,19,36) rot=(0,1,0;1.5708rad)
  Shapes = -> [Cylinder019,Cylinder018]
FEATURE [Part::Cut] Cut010  label="plugHousingTab002"
  Base = -> Box006
  Placement = pos=(-107.4,-14,0) rot=(0,0,1;0rad)
  Tool = -> Fusion036
FEATURE [Part::MultiFuse] Fusion037
  Placement = pos=(9.6,23,0) rot=(0,0,1;3.14159rad)
  Shapes = -> [Cut009,Cut010]
FEATURE [Part::Box] Box  label="Cube"
  AttacherType = Attacher::AttachEngine3D
  Height = 10
  Length = 3
  Placement = pos=(3.3,4,12) rot=(0,0,1;0rad)
  Width = 10
FEATURE [Part::Fillet] Fillet004
  Base = -> Fusion028
  Edges = 1 edges r=2: [Edge25]
FEATURE [Part::Fillet] Fillet005  label="plugHousing046"
  Base = -> Fillet004
  Edges = 1 edges r=2: [Edge8]
FEATURE [Part::Fillet] Fillet006
  Base = -> Box
  Edges = 1 edges r=2: [Edge11]
FEATURE [Part::Box] Box007  label="Cube007"
  AttacherType = Attacher::AttachEngine3D
  Height = 10
  Length = 3
  Placement = pos=(3.3,4,50) rot=(0,0,1;0rad)
  Width = 10
FEATURE [Part::Fillet] Fillet007
  Base = -> Box007
  Edges = 1 edges r=2: [Edge12]
FEATURE [Part::Box] Box008  label="Cube008"
  AttacherType = Attacher::AttachEngine3D
  Height = 28
  Length = 4
  Placement = pos=(5,0,22) rot=(0,0,1;0rad)
  Width = 10
FEATURE [Part::Fillet] Fillet008
  Base = -> Box008
  Edges = 1 edges r=1: [Edge7]
FEATURE [Part::Fillet] Fillet009
  Base = -> Fillet008
  Edges = 1 edges r=2: [Edge5]
FEATURE [Part::Fillet] Fillet010
  Base = -> Fillet009
  Edges = 1 edges r=2: [Edge2]
FEATURE [Sketcher::SketchObject] Sketch009  label="topSketch003"
  FullyConstrained = true
  sketch-geometry (4):
    g0: LineSegment StartX=16.8446 StartY=31.512 StartZ=0 EndX=16.3251 EndY=34.4666 EndZ=0
    g1: ArcOfCircle CenterX=19 CenterY=19.2524 CenterZ=0 NormalX=0 NormalY=0 NormalZ=1 AngleXU=0 Radius=15.4476 StartAngle=1.74483 EndAngle=2.72717
    g2: ArcOfCircle CenterX=19 CenterY=19.2524 CenterZ=0 NormalX=0 NormalY=0 NormalZ=1 AngleXU=0 Radius=12.4476 StartAngle=1.74483 EndAngle=2.73189
    g3: LineSegment StartX=4.86004 StartY=25.4725 StartZ=0 EndX=7.58253 EndY=24.2107 EndZ=0
  constraints (7):
    c: Block(g0)
    c: Coincident(g1,g0)
    c: Coincident(g2,g0)
    c: Coincident(g3,g1)
    c: Coincident(g3,g2)
    c: Block(g1)
    c: Block(g2)
FEATURE [Part::Extrusion] Extrude008
  Base = -> Sketch009
  Dir = (0,0,1)
  DirMode = 2
  FaceMakerClass = Part::FaceMakerBullseye
  LengthFwd = 10
  LengthRev = 0
  Placement = pos=(0,0,31) rot=(0,0,1;0rad)
  Solid = true
  Symmetric = false
FEATURE [Part::Cylinder] Cylinder020
  Angle = 360
  AttacherType = Attacher::AttachEngine3D
  Height = 20
  Placement = pos=(0,0,36.15) rot=(0,0,1;0rad)
  Radius = 8.2
FEATURE [Part::Cylinder] Cylinder021
  Angle = 360
  AttacherType = Attacher::AttachEngine3D
  Height = 10
  Placement = pos=(0,0,36.15) rot=(0,0,1;0rad)
  Radius = 4
FEATURE [Part::MultiFuse] Fusion038  label="removeToCreteHoleForPlugHousing007"
  Placement = pos=(-42,19,36) rot=(0,1,0;1.5708rad)
  Shapes = -> [Cylinder020,Cylinder021]
FEATURE [Part::Cut] Cut011
  Base = -> Extrude008
  Tool = -> Fusion038
FEATURE [Part::Fillet] Fillet011
  Base = -> Cut011
  Edges = 1 edges r=2: [Edge1]
FEATURE [Part::Fillet] Fillet012
  Base = -> Fillet011
  Edges = 1 edges r=2.5: [Edge1]
FEATURE [Part::Fillet] Fillet013
  Base = -> Fillet012
  Edges = 1 edges r=2.5: [Edge2]
FEATURE [Part::Box] Box010  label="Cube010"
  AttacherType = Attacher::AttachEngine3D
  Height = 16
  Length = 8
  Placement = pos=(12.7,31.52,28) rot=(0,0,1;0rad)
  Width = 4
FEATURE [Sketcher::SketchObject] Sketch010  label="topSketch004"
  FullyConstrained = true
  sketch-geometry (4):
    g0: LineSegment StartX=16.8446 StartY=31.512 StartZ=0 EndX=16.3251 EndY=34.4666 EndZ=0
    g1: ArcOfCircle CenterX=19 CenterY=19.2524 CenterZ=0 NormalX=0 NormalY=0 NormalZ=1 AngleXU=0 Radius=15.4476 StartAngle=1.74483 EndAngle=2.72717
    g2: ArcOfCircle CenterX=19 CenterY=19.2524 CenterZ=0 NormalX=0 NormalY=0 NormalZ=1 AngleXU=0 Radius=12.4476 StartAngle=1.74483 EndAngle=2.73189
    g3: LineSegment StartX=4.86004 StartY=25.4725 StartZ=0 EndX=7.58253 EndY=24.2107 EndZ=0
  constraints (7):
    c: Block(g0)
    c: Coincident(g1,g0)
    c: Coincident(g2,g0)
    c: Coincident(g3,g1)
    c: Coincident(g3,g2)
    c: Block(g1)
    c: Block(g2)
FEATURE [Part::Cylinder] Cylinder022
  Angle = 360
  AttacherType = Attacher::AttachEngine3D
  Height = 10
  Placement = pos=(0,0,36.15) rot=(0,0,1;0rad)
  Radius = 4
FEATURE [Sketcher::SketchObject] Sketch011  label="topSketch005"
  FullyConstrained = true
  sketch-geometry (4):
    g0: LineSegment StartX=16.8446 StartY=31.512 StartZ=0 EndX=16.3251 EndY=34.4666 EndZ=0
    g1: ArcOfCircle CenterX=19 CenterY=19.2524 CenterZ=0 NormalX=0 NormalY=0 NormalZ=1 AngleXU=0 Radius=15.4476 StartAngle=1.74483 EndAngle=2.72717
    g2: ArcOfCircle CenterX=19 CenterY=19.2524 CenterZ=0 NormalX=0 NormalY=0 NormalZ=1 AngleXU=0 Radius=12.4476 StartAngle=1.74483 EndAngle=2.73189
    g3: LineSegment StartX=4.86004 StartY=25.4725 StartZ=0 EndX=7.58253 EndY=24.2107 EndZ=0
  constraints (7):
    c: Block(g0)
    c: Coincident(g1,g0)
    c: Coincident(g2,g0)
    c: Coincident(g3,g1)
    c: Coincident(g3,g2)
    c: Block(g1)
    c: Block(g2)
FEATURE [Part::Extrusion] Extrude010
  Base = -> Sketch011
  Dir = (0,0,1)
  DirMode = 2
  FaceMakerClass = Part::FaceMakerBullseye
  LengthFwd = 10.6
  LengthRev = 0
  Placement = pos=(0,0,31) rot=(0,0,1;0rad)
  Solid = true
  Symmetric = false
FEATURE [Part::Cylinder] Cylinder023
  Angle = 360
  AttacherType = Attacher::AttachEngine3D
  Height = 20
  Placement = pos=(0,0,36.15) rot=(0,0,1;0rad)
  Radius = 8.2
FEATURE [Part::MultiFuse] Fusion039  label="removeToCreteHoleForPlugHousing008"
  Placement = pos=(-42,19,36) rot=(0,1,0;1.5708rad)
  Shapes = -> [Cylinder023,Cylinder022]
FEATURE [Part::Cut] Cut012
  Base = -> Extrude010
  Placement = pos=(0,0,-0.3) rot=(0,0,1;0rad)
  Tool = -> Fusion039
FEATURE [Part::Cut] Cut013
  Base = -> Box010
  Tool = -> Cut012
FEATURE [Part::Fillet] Fillet014
  Base = -> Cut013
  Edges = 1 edges r=0.7: [Edge13]
FEATURE [Part::Fillet] Fillet015
  Base = -> Fillet014
  Edges = 1 edges r=0.7: [Edge13]
FEATURE [Part::Fillet] Fillet016
  Base = -> Fillet015
  Edges = 1 edges r=0.7: [Edge16]
FEATURE [Part::Fillet] Fillet017
  Base = -> Fillet016
  Edges = 1 edges r=0.7: [Edge11]
FEATURE [Part::Fillet] Fillet018
  Base = -> Fillet017
  Edges = 1 edges r=0.7: [Edge10]
FEATURE [Part::Fillet] Fillet019
  Base = -> Fillet018
  Edges = 1 edges r=1.2: [Edge5]
FEATURE [Part::Fillet] Fillet020
  Base = -> Fillet019
  Edges = 1 edges r=1.2: [Edge12]
FEATURE [Part::Fillet] Fillet021
  Base = -> Fillet020
  Edges = 1 edges r=2: [Edge1]
  Placement = pos=(0.3,0,0) rot=(0,0,1;0rad)
FEATURE [Part::MultiFuse] Fusion040  label="top005"
  Shapes = -> [Cut008,Fillet021]
FEATURE [Part::MultiFuse] Fusion041  label="wireHolder"
  Shapes = -> [Fusion033,Fillet013]
FEATURE [Part::MultiFuse] Fusion042
  Shapes = -> [Fillet007,Fusion041]
FEATURE [Part::MultiFuse] Fusion043  label="wireHolder001"
  Shapes = -> [Fusion042,Fillet010]
FEATURE [Part::MultiFuse] Fusion044  label="wireHolder002"
  Shapes = -> [Fillet006,Fusion037,Fusion043]
FEATURE [Part::Feature] Face026
  shape: bbox 11 x 6 x 2e-07 mm, 1 faces, 0 solids (baked)
FEATURE [Part::Revolution] Revolve026
  Angle = 360
  Axis = (0,1,0)
  Base = (0,0,0)
  FaceMakerClass = Part::FaceMakerBullseye
  Placement = pos=(30.3,-1,19.7) rot=(0,0,1;0rad)
  Solid = false
  Source = -> Face026
  Symmetric = false
FEATURE [Sketcher::SketchObject] Sketch013  label="topSketch006"
  FullyConstrained = true
  sketch-geometry (13):
    g0: LineSegment StartX=117 StartY=19 StartZ=0 EndX=117 EndY=38 EndZ=0
    g1: ArcOfCircle CenterX=98 CenterY=19 CenterZ=0 NormalX=0 NormalY=0 NormalZ=1 AngleXU=0 Radius=19 StartAngle=5.7297 EndAngle=6.28319
    g2: LineSegment StartX=0 StartY=3 StartZ=0 EndX=0 EndY=19 EndZ=0
    g3: LineSegment StartX=19 StartY=38 StartZ=0 EndX=117 EndY=38 EndZ=0
    g4: ArcOfCircle CenterX=19 CenterY=19 CenterZ=0 NormalX=0 NormalY=0 NormalZ=1 AngleXU=0 Radius=19 StartAngle=1.5708 EndAngle=3.14159
    g5: ArcOfCircle CenterX=19 CenterY=19 CenterZ=0 NormalX=0 NormalY=0 NormalZ=1 AngleXU=0 Radius=16 StartAngle=1.5708 EndAngle=3.14159
    g6: ArcOfCircle CenterX=98 CenterY=19 CenterZ=0 NormalX=0 NormalY=0 NormalZ=1 AngleXU=0 Radius=16 StartAngle=5.60905 EndAngle=6.28319
    g7: LineSegment StartX=114 StartY=19 StartZ=0 EndX=114 EndY=35 EndZ=0
    g8: LineSegment StartX=110.5 StartY=9.01251 StartZ=0 EndX=114.163 EndY=9.01251 EndZ=0
    g9: LineSegment StartX=114 StartY=35 StartZ=0 EndX=19 EndY=35 EndZ=0
    g10: LineSegment StartX=0 StartY=3 StartZ=0 EndX=0 EndY=0 EndZ=0
    g11: LineSegment StartX=3 StartY=0 StartZ=0 EndX=0 EndY=0 EndZ=0
    g12: LineSegment StartX=3 StartY=19 StartZ=0 EndX=3 EndY=0 EndZ=0
  constraints (33):
    c: Vertical(g0)
    c: Distance(g0) = 19
    c: Block(g0)
    c: Coincident(g1,g0)
    c: Block(g1)
    c: Vertical(g2)
    c: Block(g2)
    c: Coincident(g3,g0)
    c: Horizontal(g3)
    c: Distance(g3) = 98
    c: Coincident(g4,g3)
    c: Coincident(g4,g2)
    c: Block(g4)
    c: Coincident(g5,g4)
    c: Coincident(g6,g1)
    c: Block(g6)
    c: Block(g5)
    c: Coincident(g7,g6)
    c: Vertical(g7)
    c: Coincident(g8,g6)
    c: Coincident(g8,g1)
    c: Coincident(g9,g7)
    c: Coincident(g9,g5)
    c: Horizontal(g9)
    c: Tangent(g9,g5)
    c: Coincident(g10,g2)
    c: Distance(g10) = 3
    c: Vertical(g10)
    c: Coincident(g11,g10)
    c: Horizontal(g11)
    c: Coincident(g12,g5)
    c: Coincident(g12,g11)
    c: Vertical(g12)
FEATURE [Part::Extrusion] Extrude011  label="top006"
  Base = -> Sketch013
  Dir = (0,0,1)
  DirMode = 2
  FaceMakerClass = Part::FaceMakerBullseye
  LengthFwd = 72
  LengthRev = 0
  Solid = true
  Symmetric = false
FEATURE [Sketcher::SketchObject] Sketch014
  FullyConstrained = true
  MapMode = 3
  Placement = pos=(0,0,0) rot=(1,0,0;1.5708rad)
  Support = -> [Extrude011]
  sketch-geometry (8):
    g0: Circle CenterX=80.351 CenterY=-67.6202 CenterZ=0 NormalX=0 NormalY=0 NormalZ=1 AngleXU=0 Radius=2
    g1: Circle CenterX=80.351 CenterY=-67.6202 CenterZ=0 NormalX=0 NormalY=0 NormalZ=1 AngleXU=0 Radius=3
    g2: Circle CenterX=80.351 CenterY=-4.92017 CenterZ=0 NormalX=0 NormalY=0 NormalZ=1 AngleXU=0 Radius=2
    g3: Circle CenterX=80.351 CenterY=-4.92017 CenterZ=0 NormalX=0 NormalY=0 NormalZ=1 AngleXU=0 Radius=3
    g4: Circle CenterX=23.851 CenterY=-4.92017 CenterZ=0 NormalX=0 NormalY=0 NormalZ=1 AngleXU=0 Radius=2
    g5: Circle CenterX=23.851 CenterY=-4.92017 CenterZ=0 NormalX=0 NormalY=0 NormalZ=1 AngleXU=0 Radius=3
    g6: Circle CenterX=23.851 CenterY=-67.6202 CenterZ=0 NormalX=0 NormalY=0 NormalZ=1 AngleXU=0 Radius=2
    g7: Circle CenterX=23.851 CenterY=-67.6202 CenterZ=0 NormalX=0 NormalY=0 NormalZ=1 AngleXU=0 Radius=3
  constraints (8):
    c: Block(g3)
    c: Block(g2)
    c: Block(g1)
    c: Block(g0)
    c: Block(g6)
    c: Block(g7)
    c: Block(g4)
    c: Block(g5)
FEATURE [Part::Feature] Face027
  shape: bbox 11 x 6 x 2e-07 mm, 1 faces, 0 solids (baked)
FEATURE [Part::Revolution] Revolve027
  Angle = 360
  Axis = (0,1,0)
  Base = (0,0,0)
  FaceMakerClass = Part::FaceMakerBullseye
  Placement = pos=(30.3,-1,51.7) rot=(0,0,1;0rad)
  Solid = false
  Source = -> Face027
  Symmetric = false
FEATURE [Part::Feature] Face028
  shape: bbox 11 x 6 x 2e-07 mm, 1 faces, 0 solids (baked)
FEATURE [Part::Revolution] Revolve028
  Angle = 360
  Axis = (0,1,0)
  Base = (0,0,0)
  FaceMakerClass = Part::FaceMakerBullseye
  Placement = pos=(62.3,-1,19.7) rot=(0,0,1;0rad)
  Solid = false
  Source = -> Face028
  Symmetric = false
FEATURE [Part::Feature] Face029
  shape: bbox 11 x 6 x 2e-07 mm, 1 faces, 0 solids (baked)
FEATURE [Part::Revolution] Revolve029
  Angle = 360
  Axis = (0,1,0)
  Base = (0,0,0)
  FaceMakerClass = Part::FaceMakerBullseye
  Placement = pos=(62.3,-1,51.7) rot=(0,0,1;0rad)
  Solid = false
  Source = -> Face029
  Symmetric = false
FEATURE [Part::Feature] Wire
  shape: bbox 11 x 5.2 x 2e-07 mm, 0 faces, 0 solids (baked)
FEATURE [Part::Revolution] Revolve030
  Angle = 360
  Axis = (0,1,0)
  Base = (0,0,0)
  FaceMakerClass = Part::FaceMakerBullseye
  Placement = pos=(30.3,38,19.7) rot=(0,0,1;0rad)
  Solid = true
  Source = -> Wire
  Symmetric = false
FEATURE [Part::Feature] Wire001
  shape: bbox 11 x 5.2 x 2e-07 mm, 0 faces, 0 solids (baked)
FEATURE [Part::Revolution] Revolve031
  Angle = 360
  Axis = (0,1,0)
  Base = (0,0,0)
  FaceMakerClass = Part::FaceMakerBullseye
  Placement = pos=(30.3,38,51.7) rot=(0,0,1;0rad)
  Solid = true
  Source = -> Wire001
  Symmetric = false
FEATURE [Part::Feature] Wire002
  shape: bbox 11 x 5.2 x 2e-07 mm, 0 faces, 0 solids (baked)
FEATURE [Part::Revolution] Revolve032
  Angle = 360
  Axis = (0,1,0)
  Base = (0,0,0)
  FaceMakerClass = Part::FaceMakerBullseye
  Placement = pos=(62.3,38,51.7) rot=(0,0,1;0rad)
  Solid = true
  Source = -> Wire002
  Symmetric = false
FEATURE [Part::Feature] Wire003
  shape: bbox 11 x 5.2 x 2e-07 mm, 0 faces, 0 solids (baked)
FEATURE [Part::Revolution] Revolve033
  Angle = 360
  Axis = (0,1,0)
  Base = (0,0,0)
  FaceMakerClass = Part::FaceMakerBullseye
  Placement = pos=(62.3,38,19.7) rot=(0,0,1;0rad)
  Solid = true
  Source = -> Wire003
  Symmetric = false
FEATURE [Part::MultiFuse] Fusion045  label="altRandScrewHousing"
  Shapes = -> [Revolve029,Revolve027,Revolve028,Revolve026]
FEATURE [Part::MultiFuse] Fusion046  label="fanScrewHousing"
  Shapes = -> [Revolve033,Revolve032,Revolve031,Revolve030]
FEATURE [Sketcher::SketchObject] Sketch015
  FullyConstrained = true
  sketch-geometry (17):
    g0: Circle CenterX=-3.5 CenterY=23.5 CenterZ=0 NormalX=0 NormalY=0 NormalZ=1 AngleXU=0 Radius=1
    g1: Circle CenterX=-1 CenterY=15.25 CenterZ=0 NormalX=0 NormalY=0 NormalZ=1 AngleXU=0 Radius=1
    g2: Circle CenterX=-3.5 CenterY=7 CenterZ=0 NormalX=0 NormalY=0 NormalZ=1 AngleXU=0 Radius=1
    g3: BSplineCurve PolesCount=3 KnotsCount=2 Degree=2 IsPeriodic=0
    g4: GeomPoint X=-3.5 Y=23.5 Z=0
    g5: GeomPoint X=-3.5 Y=7 Z=0
    g6: Circle CenterX=-4.8 CenterY=30.5 CenterZ=0 NormalX=0 NormalY=0 NormalZ=1 AngleXU=0 Radius=1
    g7: Circle CenterX=-3.5 CenterY=30.5 CenterZ=0 NormalX=0 NormalY=0 NormalZ=1 AngleXU=0 Radius=1
    g8: Circle CenterX=-3.5 CenterY=29.2 CenterZ=0 NormalX=0 NormalY=0 NormalZ=1 AngleXU=0 Radius=1
    g9: BSplineCurve PolesCount=3 KnotsCount=2 Degree=2 IsPeriodic=0
    g10: GeomPoint X=-4.8 Y=30.5 Z=0
    g11: GeomPoint X=-3.5 Y=29.2 Z=0
    g12: LineSegment StartX=-3.5 StartY=29.2 StartZ=0 EndX=-3.5 EndY=23.5 EndZ=0
    g13: LineSegment StartX=-4.8 StartY=30.5 StartZ=0 EndX=0 EndY=30.5 EndZ=0
    g14: LineSegment StartX=-3.5 StartY=0.3 StartZ=0 EndX=0 EndY=0.3 EndZ=0
    g15: LineSegment StartX=-3.5 StartY=0.3 StartZ=0 EndX=-3.5 EndY=7 EndZ=0
    g16: LineSegment StartX=0 StartY=0.3 StartZ=0 EndX=0 EndY=30.5 EndZ=0
  constraints (33):
    c: Weight(g0) = 1
    c: Equal(g0,g1)
    c: Equal(g0,g2)
    c: InternalAlignment(g0,g3)
    c: InternalAlignment(g1,g3)
    c: InternalAlignment(g2,g3)
    c: InternalAlignment(g4,g3)
    c: InternalAlignment(g5,g3)
    c: Block(g3)
    c: Weight(g6) = 1
    c: Equal(g6,g7)
    c: Equal(g6,g8)
    c: InternalAlignment(g6,g9)
    c: InternalAlignment(g7,g9)
    c: InternalAlignment(g8,g9)
    c: InternalAlignment(g10,g9)
    c: InternalAlignment(g11,g9)
    c: Block(g9)
    c: Coincident(g12,g9)
    c: Coincident(g12,g3)
    c: Vertical(g12)
    c: Coincident(g13,g9)
    c: Horizontal(g13)
    c: Distance(g13) = 4.8
    c: Horizontal(g14)
    c: Block(g14)
    c: Coincident(g15,g14)
    c: Coincident(g15,g3)
    c: Vertical(g15)
    c: Coincident(g16,g14)
    c: Coincident(g16,g13)
    c: Vertical(g16)
    c: Tangent(g16,g1)
FEATURE [Sketcher::SketchObject] Sketch016
  FullyConstrained = true
  sketch-geometry (16):
    g0: Circle CenterX=-3.5 CenterY=23.5 CenterZ=0 NormalX=0 NormalY=0 NormalZ=1 AngleXU=0 Radius=1
    g1: Circle CenterX=-1 CenterY=15.25 CenterZ=0 NormalX=0 NormalY=0 NormalZ=1 AngleXU=0 Radius=1
    g2: Circle CenterX=-3.5 CenterY=7 CenterZ=0 NormalX=0 NormalY=0 NormalZ=1 AngleXU=0 Radius=1
    g3: BSplineCurve PolesCount=3 KnotsCount=2 Degree=2 IsPeriodic=0
    g4: GeomPoint X=-3.5 Y=23.5 Z=0
    g5: GeomPoint X=-3.5 Y=7 Z=0
    g6: LineSegment StartX=-3.5 StartY=28.2 StartZ=0 EndX=-3.5 EndY=23.5 EndZ=0
    g7: LineSegment StartX=0 StartY=29.5 StartZ=0 EndX=0 EndY=30 EndZ=0
    g8: LineSegment StartX=-3.5 StartY=28.2 StartZ=0 EndX=-3.5 EndY=30 EndZ=0
    g9: LineSegment StartX=0 StartY=30 StartZ=0 EndX=0 EndY=30.5 EndZ=0
    g10: LineSegment StartX=0 StartY=30.5 StartZ=0 EndX=-3.5 EndY=30.5 EndZ=0
    g11: LineSegment StartX=-3.5 StartY=30.5 StartZ=0 EndX=-3.5 EndY=30 EndZ=0
    g12: LineSegment StartX=0 StartY=29.5 StartZ=0 EndX=0 EndY=5 EndZ=0
    g13: LineSegment StartX=-3.5 StartY=0.3 StartZ=0 EndX=-3.5 EndY=7 EndZ=0
    g14: LineSegment StartX=-3.5 StartY=0.3 StartZ=0 EndX=0 EndY=0.3 EndZ=0
    g15: LineSegment StartX=0 StartY=5 StartZ=0 EndX=0 EndY=0.3 EndZ=0
  constraints (39):
    c: Weight(g0) = 1
    c: Equal(g0,g1)
    c: Equal(g0,g2)
    c: InternalAlignment(g0,g3)
    c: InternalAlignment(g1,g3)
    c: InternalAlignment(g2,g3)
    c: InternalAlignment(g4,g3)
    c: InternalAlignment(g5,g3)
    c: Block(g3)
    c: Coincident(g6,g3)
    c: Vertical(g6)
    c: Vertical(g7)
    c: Distance(g7) = 0.5
    c: Coincident(g8,g6)
    c: Vertical(g8)
    c: Block(g6)
    c: Block(g7)
    c: Vertical(g9)
    c: Equal(g7,g9) = 0.5
    c: Block(g9)
    c: Coincident(g9,g7)
    c: Horizontal(g10)
    c: Coincident(g10,g9)
    c: Coincident(g11,g10)
    c: Coincident(g11,g8)
    c: Vertical(g11)
    c: Block(g11)
    c: Coincident(g12,g7)
    c: Vertical(g12)
    c: Coincident(g13,g3)
    c: Vertical(g13)
    c: Distance(g13) = 6.7
    c: Coincident(g14,g13)
    c: Horizontal(g14)
    c: Block(g14)
    c: Coincident(g15,g12)
    c: Coincident(g15,g14)
    c: Vertical(g15)
    c: Block(g15)
FEATURE [Sketcher::SketchObject] Sketch017
  FullyConstrained = true
  sketch-geometry (11):
    g0: LineSegment StartX=-3.5 StartY=1e-16 StartZ=0 EndX=-1.6 EndY=1e-16 EndZ=0
    g1: LineSegment StartX=-1.6 StartY=1e-16 StartZ=0 EndX=-1.6 EndY=1.5 EndZ=0
    g2: LineSegment StartX=-3.5 StartY=1.5 StartZ=0 EndX=-1.6 EndY=1.5 EndZ=0
    g3: LineSegment StartX=-3.5 StartY=1e-16 StartZ=0 EndX=-4.8 EndY=1e-16 EndZ=0
    g4: Circle CenterX=-3.5 CenterY=1.3 CenterZ=0 NormalX=0 NormalY=0 NormalZ=1 AngleXU=0 Radius=1
    g5: Circle CenterX=-3.5 CenterY=1e-16 CenterZ=0 NormalX=0 NormalY=0 NormalZ=1 AngleXU=0 Radius=1
    g6: Circle CenterX=-4.8 CenterY=1e-16 CenterZ=0 NormalX=0 NormalY=0 NormalZ=1 AngleXU=0 Radius=1
    g7: BSplineCurve PolesCount=3 KnotsCount=2 Degree=2 IsPeriodic=0
    g8: GeomPoint X=-3.5 Y=1.3 Z=0
    g9: GeomPoint X=-4.8 Y=1e-16 Z=0
    g10: LineSegment StartX=-3.5 StartY=1.3 StartZ=0 EndX=-3.5 EndY=1.5 EndZ=0
  constraints (24):
    c: Horizontal(g0)
    c: Distance(g0) = 1.9
    c: Block(g0)
    c: Coincident(g1,g0)
    c: Vertical(g1)
    c: Coincident(g2,g1)
    c: Horizontal(g2)
    c: Coincident(g3,g0)
    c: Horizontal(g3)
    c: Distance(g3) = 1.3
    c: Weight(g4) = 1
    c: Equal(g4,g5)
    c: Coincident(g5,g0)
    c: Equal(g4,g6)
    c: Coincident(g7,g3)
    c: InternalAlignment(g4,g7)
    c: InternalAlignment(g5,g7)
    c: InternalAlignment(g6,g7)
    c: InternalAlignment(g8,g7)
    c: InternalAlignment(g9,g7)
    c: Coincident(g10,g7)
    c: Coincident(g10,g2)
    c: Vertical(g10)
    c: Block(g10)
FEATURE [Part::Feature] Face035
  shape: bbox 3.2 x 1.5 x 2e-07 mm, 1 faces, 0 solids (baked)
FEATURE [Part::Revolution] Revolve039  label="backCaseScrewRetainer"
  Angle = 360
  Axis = (0,1,0)
  Base = (0,0,0)
  FaceMakerClass = Part::FaceMakerBullseye
  Placement = pos=(12.5,3,62) rot=(0,0,1;0rad)
  Solid = false
  Source = -> Face035
  Symmetric = false
FEATURE [Part::Feature] Face036
  shape: bbox 3.2 x 1.5 x 2e-07 mm, 1 faces, 0 solids (baked)
FEATURE [Part::Feature] Face039
  shape: bbox 4.8 x 30.2 x 2e-07 mm, 1 faces, 0 solids (baked)
FEATURE [Part::Revolution] Revolve043  label="frontCaseScrewPost002"
  Angle = 360
  Axis = (0,1,0)
  Base = (0,0,0)
  FaceMakerClass = Part::FaceMakerBullseye
  Placement = pos=(89.5,4.5,3.5) rot=(0,0,1;0rad)
  Solid = false
  Source = -> Face039
  Symmetric = false
FEATURE [Part::Feature] Face042
  shape: bbox 4.8 x 30.2 x 2e-07 mm, 1 faces, 0 solids (baked)
FEATURE [Part::Revolution] Revolve046  label="frontCaseScrewPost003"
  Angle = 360
  Axis = (0,1,0)
  Base = (0,0,0)
  FaceMakerClass = Part::FaceMakerBullseye
  Placement = pos=(89.5,4.5,68.5) rot=(0,0,1;0rad)
  Solid = false
  Source = -> Face042
  Symmetric = false
FEATURE [Part::Feature] Face043
  shape: bbox 3.2 x 1.5 x 2e-07 mm, 1 faces, 0 solids (baked)
FEATURE [Part::Revolution] Revolve047  label="frontCaseScrewRetainer002"
  Angle = 360
  Axis = (0,1,0)
  Base = (0,0,0)
  FaceMakerClass = Part::FaceMakerBullseye
  Placement = pos=(89.5,3,68.5) rot=(0,0,1;0rad)
  Solid = false
  Source = -> Face043
  Symmetric = false
FEATURE [Part::Feature] Face044
  shape: bbox 3.2 x 1.5 x 2e-07 mm, 1 faces, 0 solids (baked)
FEATURE [Part::Revolution] Revolve048  label="frontCaseScrewRetainer003"
  Angle = 360
  Axis = (0,1,0)
  Base = (0,0,0)
  FaceMakerClass = Part::FaceMakerBullseye
  Placement = pos=(89.5,3,3.5) rot=(0,0,1;0rad)
  Solid = false
  Source = -> Face044
  Symmetric = false
FEATURE [App::MeasureDistance] Distance002  label="Distance: 1.67 mm"
  Distance = 1.66921
  P1 = (99.2361,4.7524,71.7)
  P2 = (99.2347,6.42161,71.7)
FEATURE [Sketcher::SketchObject] Sketch018
  FullyConstrained = true
  sketch-geometry (7):
    g0: LineSegment StartX=0 StartY=0 StartZ=0 EndX=0 EndY=6 EndZ=0
    g1: Circle CenterX=0 CenterY=0 CenterZ=0 NormalX=0 NormalY=0 NormalZ=1 AngleXU=0 Radius=1
    g2: Circle CenterX=8 CenterY=6 CenterZ=0 NormalX=0 NormalY=0 NormalZ=1 AngleXU=0 Radius=1
    g3: BSplineCurve PolesCount=3 KnotsCount=2 Degree=2 IsPeriodic=0
    g4: GeomPoint X=0 Y=0 Z=0
    g5: GeomPoint X=8 Y=6 Z=0
    g6: LineSegment StartX=0 StartY=6 StartZ=0 EndX=8 EndY=6 EndZ=0
  constraints (14):
    c: Coincident(g0,g-1)
    c: Distance(g0) = 6
    c: Vertical(g0)
    c: Coincident(g3,g0)
    c: Weight(g1) = 1
    c: Equal(g1,g2)
    c: InternalAlignment(g1,g3)
    c: InternalAlignment(g2,g3)
    c: InternalAlignment(g4,g3)
    c: InternalAlignment(g5,g3)
    c: Block(g3)
    c: Coincident(g6,g0)
    c: Coincident(g6,g3)
    c: Horizontal(g6)
FEATURE [Part::Extrusion] Extrude012  label="caseScrewPillarBracket"
  Base = -> Sketch018
  Dir = (0,0,1)
  DirMode = 2
  FaceMakerClass = Part::FaceMakerBullseye
  LengthFwd = 2.4
  LengthRev = 0
  Placement = pos=(15.76,29,8.8) rot=(0,1,0;0rad)
  Solid = true
  Symmetric = false
FEATURE [Sketcher::SketchObject] Sketch019
  FullyConstrained = true
  sketch-geometry (7):
    g0: LineSegment StartX=0 StartY=0 StartZ=0 EndX=0 EndY=6 EndZ=0
    g1: Circle CenterX=0 CenterY=0 CenterZ=0 NormalX=0 NormalY=0 NormalZ=1 AngleXU=0 Radius=1
    g2: Circle CenterX=8 CenterY=6 CenterZ=0 NormalX=0 NormalY=0 NormalZ=1 AngleXU=0 Radius=1
    g3: BSplineCurve PolesCount=3 KnotsCount=2 Degree=2 IsPeriodic=0
    g4: GeomPoint X=0 Y=0 Z=0
    g5: GeomPoint X=8 Y=6 Z=0
    g6: LineSegment StartX=0 StartY=6 StartZ=0 EndX=8 EndY=6 EndZ=0
  constraints (14):
    c: Coincident(g0,g-1)
    c: Distance(g0) = 6
    c: Vertical(g0)
    c: Coincident(g3,g0)
    c: Weight(g1) = 1
    c: Equal(g1,g2)
    c: InternalAlignment(g1,g3)
    c: InternalAlignment(g2,g3)
    c: InternalAlignment(g4,g3)
    c: InternalAlignment(g5,g3)
    c: Block(g3)
    c: Coincident(g6,g0)
    c: Coincident(g6,g3)
    c: Horizontal(g6)
FEATURE [Part::Extrusion] Extrude013  label="caseScrewPillarBracket001"
  Base = -> Sketch019
  Dir = (0,0,1)
  DirMode = 2
  FaceMakerClass = Part::FaceMakerBullseye
  LengthFwd = 2.4
  LengthRev = 0
  Placement = pos=(15.76,29,60.8) rot=(0,0,1;0rad)
  Solid = true
  Symmetric = false
FEATURE [Sketcher::SketchObject] Sketch020
  FullyConstrained = true
  sketch-geometry (7):
    g0: LineSegment StartX=0 StartY=0 StartZ=0 EndX=0 EndY=6 EndZ=0
    g1: Circle CenterX=0 CenterY=0 CenterZ=0 NormalX=0 NormalY=0 NormalZ=1 AngleXU=0 Radius=1
    g2: Circle CenterX=8 CenterY=6 CenterZ=0 NormalX=0 NormalY=0 NormalZ=1 AngleXU=0 Radius=1
    g3: BSplineCurve PolesCount=3 KnotsCount=2 Degree=2 IsPeriodic=0
    g4: GeomPoint X=0 Y=0 Z=0
    g5: GeomPoint X=8 Y=6 Z=0
    g6: LineSegment StartX=0 StartY=6 StartZ=0 EndX=8 EndY=6 EndZ=0
  constraints (14):
    c: Coincident(g0,g-1)
    c: Distance(g0) = 6
    c: Vertical(g0)
    c: Coincident(g3,g0)
    c: Weight(g1) = 1
    c: Equal(g1,g2)
    c: InternalAlignment(g1,g3)
    c: InternalAlignment(g2,g3)
    c: InternalAlignment(g4,g3)
    c: InternalAlignment(g5,g3)
    c: Block(g3)
    c: Coincident(g6,g0)
    c: Coincident(g6,g3)
    c: Horizontal(g6)
FEATURE [Part::Extrusion] Extrude014  label="caseScrewPillarBracket002"
  Base = -> Sketch020
  Dir = (0,0,1)
  DirMode = 2
  FaceMakerClass = Part::FaceMakerBullseye
  LengthFwd = 2.4
  LengthRev = 0
  Placement = pos=(13.7,29,13.26) rot=(0,1,0;-1.5708rad)
  Solid = true
  Symmetric = false
FEATURE [Sketcher::SketchObject] Sketch021
  FullyConstrained = true
  sketch-geometry (7):
    g0: LineSegment StartX=0 StartY=0 StartZ=0 EndX=0 EndY=6 EndZ=0
    g1: Circle CenterX=0 CenterY=0 CenterZ=0 NormalX=0 NormalY=0 NormalZ=1 AngleXU=0 Radius=1
    g2: Circle CenterX=8 CenterY=6 CenterZ=0 NormalX=0 NormalY=0 NormalZ=1 AngleXU=0 Radius=1
    g3: BSplineCurve PolesCount=3 KnotsCount=2 Degree=2 IsPeriodic=0
    g4: GeomPoint X=0 Y=0 Z=0
    g5: GeomPoint X=8 Y=6 Z=0
    g6: LineSegment StartX=0 StartY=6 StartZ=0 EndX=8 EndY=6 EndZ=0
  constraints (14):
    c: Coincident(g0,g-1)
    c: Distance(g0) = 6
    c: Vertical(g0)
    c: Coincident(g3,g0)
    c: Weight(g1) = 1
    c: Equal(g1,g2)
    c: InternalAlignment(g1,g3)
    c: InternalAlignment(g2,g3)
    c: InternalAlignment(g4,g3)
    c: InternalAlignment(g5,g3)
    c: Block(g3)
    c: Coincident(g6,g0)
    c: Coincident(g6,g3)
    c: Horizontal(g6)
FEATURE [Part::Extrusion] Extrude015  label="caseScrewPillarBracket003"
  Base = -> Sketch021
  Dir = (0,0,1)
  DirMode = 2
  FaceMakerClass = Part::FaceMakerBullseye
  LengthFwd = 2.4
  LengthRev = 0
  Placement = pos=(11.3,29,58.74) rot=(0,1,0;1.5708rad)
  Solid = true
  Symmetric = false
FEATURE [Sketcher::SketchObject] Sketch022
  FullyConstrained = true
  sketch-geometry (7):
    g0: LineSegment StartX=0 StartY=0 StartZ=0 EndX=0 EndY=6 EndZ=0
    g1: Circle CenterX=0 CenterY=0 CenterZ=0 NormalX=0 NormalY=0 NormalZ=1 AngleXU=0 Radius=1
    g2: Circle CenterX=8 CenterY=6 CenterZ=0 NormalX=0 NormalY=0 NormalZ=1 AngleXU=0 Radius=1
    g3: BSplineCurve PolesCount=3 KnotsCount=2 Degree=2 IsPeriodic=0
    g4: GeomPoint X=0 Y=0 Z=0
    g5: GeomPoint X=8 Y=6 Z=0
    g6: LineSegment StartX=0 StartY=6 StartZ=0 EndX=8 EndY=6 EndZ=0
  constraints (14):
    c: Coincident(g0,g-1)
    c: Distance(g0) = 6
    c: Vertical(g0)
    c: Coincident(g3,g0)
    c: Weight(g1) = 1
    c: Equal(g1,g2)
    c: InternalAlignment(g1,g3)
    c: InternalAlignment(g2,g3)
    c: InternalAlignment(g4,g3)
    c: InternalAlignment(g5,g3)
    c: Block(g3)
    c: Coincident(g6,g0)
    c: Coincident(g6,g3)
    c: Horizontal(g6)
FEATURE [Part::Extrusion] Extrude016  label="caseScrewPillarBracket004"
  Base = -> Sketch022
  Dir = (0,0,1)
  DirMode = 2
  FaceMakerClass = Part::FaceMakerBullseye
  LengthFwd = 2.4
  LengthRev = 0
  Placement = pos=(88.3,29,65.23) rot=(0,1,0;1.5708rad)
  Solid = true
  Symmetric = false
FEATURE [Sketcher::SketchObject] Sketch023
  FullyConstrained = true
  sketch-geometry (7):
    g0: LineSegment StartX=0 StartY=0 StartZ=0 EndX=0 EndY=6 EndZ=0
    g1: Circle CenterX=0 CenterY=0 CenterZ=0 NormalX=0 NormalY=0 NormalZ=1 AngleXU=0 Radius=1
    g2: Circle CenterX=8 CenterY=6 CenterZ=0 NormalX=0 NormalY=0 NormalZ=1 AngleXU=0 Radius=1
    g3: BSplineCurve PolesCount=3 KnotsCount=2 Degree=2 IsPeriodic=0
    g4: GeomPoint X=0 Y=0 Z=0
    g5: GeomPoint X=8 Y=6 Z=0
    g6: LineSegment StartX=0 StartY=6 StartZ=0 EndX=8 EndY=6 EndZ=0
  constraints (14):
    c: Coincident(g0,g-1)
    c: Distance(g0) = 6
    c: Vertical(g0)
    c: Coincident(g3,g0)
    c: Weight(g1) = 1
    c: Equal(g1,g2)
    c: InternalAlignment(g1,g3)
    c: InternalAlignment(g2,g3)
    c: InternalAlignment(g4,g3)
    c: InternalAlignment(g5,g3)
    c: Block(g3)
    c: Coincident(g6,g0)
    c: Coincident(g6,g3)
    c: Horizontal(g6)
FEATURE [Part::Extrusion] Extrude017  label="caseScrewPillarBracket005"
  Base = -> Sketch023
  Dir = (0,0,1)
  DirMode = 2
  FaceMakerClass = Part::FaceMakerBullseye
  LengthFwd = 2.4
  LengthRev = 0
  Placement = pos=(90.7,29,6.77) rot=(0,-1,0;1.5708rad)
  Solid = true
  Symmetric = false
FEATURE [Sketcher::SketchObject] Sketch024
  FullyConstrained = true
  sketch-geometry (7):
    g0: LineSegment StartX=0 StartY=0 StartZ=0 EndX=0 EndY=6 EndZ=0
    g1: Circle CenterX=0 CenterY=0 CenterZ=0 NormalX=0 NormalY=0 NormalZ=1 AngleXU=0 Radius=1
    g2: Circle CenterX=8 CenterY=6 CenterZ=0 NormalX=0 NormalY=0 NormalZ=1 AngleXU=0 Radius=1
    g3: BSplineCurve PolesCount=3 KnotsCount=2 Degree=2 IsPeriodic=0
    g4: GeomPoint X=0 Y=0 Z=0
    g5: GeomPoint X=8 Y=6 Z=0
    g6: LineSegment StartX=0 StartY=6 StartZ=0 EndX=8 EndY=6 EndZ=0
  constraints (14):
    c: Coincident(g0,g-1)
    c: Distance(g0) = 6
    c: Vertical(g0)
    c: Coincident(g3,g0)
    c: Weight(g1) = 1
    c: Equal(g1,g2)
    c: InternalAlignment(g1,g3)
    c: InternalAlignment(g2,g3)
    c: InternalAlignment(g4,g3)
    c: InternalAlignment(g5,g3)
    c: Block(g3)
    c: Coincident(g6,g0)
    c: Coincident(g6,g3)
    c: Horizontal(g6)
FEATURE [Part::Extrusion] Extrude018  label="caseScrewPillarBracket006"
  Base = -> Sketch024
  Dir = (0,0,1)
  DirMode = 2
  FaceMakerClass = Part::FaceMakerBullseye
  LengthFwd = 2.4
  LengthRev = 0
  Placement = pos=(103.7,29,6.77) rot=(0,-1,0;1.5708rad)
  Solid = true
  Symmetric = false
FEATURE [Sketcher::SketchObject] Sketch025
  FullyConstrained = true
  sketch-geometry (7):
    g0: LineSegment StartX=0 StartY=0 StartZ=0 EndX=0 EndY=6 EndZ=0
    g1: Circle CenterX=0 CenterY=0 CenterZ=0 NormalX=0 NormalY=0 NormalZ=1 AngleXU=0 Radius=1
    g2: Circle CenterX=8 CenterY=6 CenterZ=0 NormalX=0 NormalY=0 NormalZ=1 AngleXU=0 Radius=1
    g3: BSplineCurve PolesCount=3 KnotsCount=2 Degree=2 IsPeriodic=0
    g4: GeomPoint X=0 Y=0 Z=0
    g5: GeomPoint X=8 Y=6 Z=0
    g6: LineSegment StartX=0 StartY=6 StartZ=0 EndX=8 EndY=6 EndZ=0
  constraints (14):
    c: Coincident(g0,g-1)
    c: Distance(g0) = 6
    c: Vertical(g0)
    c: Coincident(g3,g0)
    c: Weight(g1) = 1
    c: Equal(g1,g2)
    c: InternalAlignment(g1,g3)
    c: InternalAlignment(g2,g3)
    c: InternalAlignment(g4,g3)
    c: InternalAlignment(g5,g3)
    c: Block(g3)
    c: Coincident(g6,g0)
    c: Coincident(g6,g3)
    c: Horizontal(g6)
FEATURE [Part::Extrusion] Extrude019  label="caseScrewPillarBracket007"
  Base = -> Sketch025
  Dir = (0,0,1)
  DirMode = 2
  FaceMakerClass = Part::FaceMakerBullseye
  LengthFwd = 2.4
  LengthRev = 0
  Placement = pos=(101.3,29,65.23) rot=(0,1,0;1.5708rad)
  Solid = true
  Symmetric = false
FEATURE [Part::Box] Box011  label="frontCaseScrewPillarBracket"
  AttacherType = Attacher::AttachEngine3D
  Height = 2.4
  Length = 16
  Placement = pos=(87,28,2.3) rot=(0,0,1;0rad)
  Width = 7
FEATURE [Part::Box] Box012  label="frontCaseScrewPillarBracket001"
  AttacherType = Attacher::AttachEngine3D
  Height = 2.4
  Length = 16
  Placement = pos=(87,28,67.3) rot=(0,0,1;0rad)
  Width = 7
FEATURE [Sketcher::SketchObject] Sketch026
  FullyConstrained = true
  sketch-geometry (17):
    g0: Circle CenterX=-3.5 CenterY=23.5 CenterZ=0 NormalX=0 NormalY=0 NormalZ=1 AngleXU=0 Radius=1
    g1: Circle CenterX=-1 CenterY=15.25 CenterZ=0 NormalX=0 NormalY=0 NormalZ=1 AngleXU=0 Radius=1
    g2: Circle CenterX=-3.5 CenterY=7 CenterZ=0 NormalX=0 NormalY=0 NormalZ=1 AngleXU=0 Radius=1
    g3: BSplineCurve PolesCount=3 KnotsCount=2 Degree=2 IsPeriodic=0
    g4: GeomPoint X=-3.5 Y=23.5 Z=0
    g5: GeomPoint X=-3.5 Y=7 Z=0
    g6: Circle CenterX=-4.8 CenterY=30.5 CenterZ=0 NormalX=0 NormalY=0 NormalZ=1 AngleXU=0 Radius=1
    g7: Circle CenterX=-3.5 CenterY=30.5 CenterZ=0 NormalX=0 NormalY=0 NormalZ=1 AngleXU=0 Radius=1
    g8: Circle CenterX=-3.5 CenterY=29.2 CenterZ=0 NormalX=0 NormalY=0 NormalZ=1 AngleXU=0 Radius=1
    g9: BSplineCurve PolesCount=3 KnotsCount=2 Degree=2 IsPeriodic=0
    g10: GeomPoint X=-4.8 Y=30.5 Z=0
    g11: GeomPoint X=-3.5 Y=29.2 Z=0
    g12: LineSegment StartX=-3.5 StartY=29.2 StartZ=0 EndX=-3.5 EndY=23.5 EndZ=0
    g13: LineSegment StartX=-4.8 StartY=30.5 StartZ=0 EndX=0 EndY=30.5 EndZ=0
    g14: LineSegment StartX=-3.5 StartY=5 StartZ=0 EndX=-3.5 EndY=7 EndZ=0
    g15: LineSegment StartX=0 StartY=5 StartZ=0 EndX=0 EndY=30.5 EndZ=0
    g16: LineSegment StartX=-3.5 StartY=5 StartZ=0 EndX=0 EndY=5 EndZ=0
  constraints (33):
    c: Weight(g0) = 1
    c: Equal(g0,g1)
    c: Equal(g0,g2)
    c: InternalAlignment(g0,g3)
    c: InternalAlignment(g1,g3)
    c: InternalAlignment(g2,g3)
    c: InternalAlignment(g4,g3)
    c: InternalAlignment(g5,g3)
    c: Block(g3)
    c: Weight(g6) = 1
    c: Equal(g6,g7)
    c: Equal(g6,g8)
    c: InternalAlignment(g6,g9)
    c: InternalAlignment(g7,g9)
    c: InternalAlignment(g8,g9)
    c: InternalAlignment(g10,g9)
    c: InternalAlignment(g11,g9)
    c: Block(g9)
    c: Coincident(g12,g9)
    c: Coincident(g12,g3)
    c: Vertical(g12)
    c: Coincident(g13,g9)
    c: Horizontal(g13)
    c: Distance(g13) = 4.8
    c: Coincident(g14,g3)
    c: Vertical(g14)
    c: Coincident(g15,g13)
    c: Vertical(g15)
    c: Tangent(g15,g1)
    c: Distance(g14) = 2
    c: Coincident(g16,g14)
    c: Horizontal(g16)
    c: Coincident(g15,g16)
FEATURE [Part::Feature] Face050
  shape: bbox 4.8 x 25.5 x 2e-07 mm, 1 faces, 0 solids (baked)
FEATURE [Part::Revolution] Revolve054  label="moreFrontCaseScrewPost001"
  Angle = 360
  Axis = (0,1,0)
  Base = (0,0,0)
  FaceMakerClass = Part::FaceMakerBullseye
  Placement = pos=(102.5,4.5,3.5) rot=(0,0,1;0rad)
  Solid = false
  Source = -> Face050
  Symmetric = false
FEATURE [Part::Feature] Face051
  shape: bbox 4.8 x 25.5 x 2e-07 mm, 1 faces, 0 solids (baked)
FEATURE [Part::Revolution] Revolve055  label="moreFrontCaseScrewPost002"
  Angle = 360
  Axis = (0,1,0)
  Base = (0,0,0)
  FaceMakerClass = Part::FaceMakerBullseye
  Placement = pos=(102.5,4.5,68.5) rot=(0,0,1;0rad)
  Solid = false
  Source = -> Face051
  Symmetric = false
FEATURE [Sketcher::SketchObject] Sketch027
  FullyConstrained = true
  sketch-geometry (10):
    g0: LineSegment StartX=-1.6 StartY=4.7 StartZ=0 EndX=-1.6 EndY=1.7 EndZ=0
    g1: LineSegment StartX=-3.5 StartY=4.7 StartZ=0 EndX=-1.6 EndY=4.7 EndZ=0
    g2: LineSegment StartX=-1.6 StartY=1.7 StartZ=0 EndX=-1.6 EndY=1.5 EndZ=0
    g3: LineSegment StartX=-1.6 StartY=1.5 StartZ=0 EndX=-5.2 EndY=1.5 EndZ=0
    g4: Circle CenterX=-3.5 CenterY=4.7 CenterZ=0 NormalX=0 NormalY=0 NormalZ=1 AngleXU=0 Radius=1
    g5: Circle CenterX=-3.59627 CenterY=2.99743 CenterZ=0 NormalX=0 NormalY=0 NormalZ=1 AngleXU=0 Radius=1
    g6: Circle CenterX=-5.2 CenterY=1.5 CenterZ=0 NormalX=0 NormalY=0 NormalZ=1 AngleXU=0 Radius=1
    g7: BSplineCurve PolesCount=3 KnotsCount=2 Degree=2 IsPeriodic=0
    g8: GeomPoint X=-3.5 Y=4.7 Z=0
    g9: GeomPoint X=-5.2 Y=1.5 Z=0
  constraints (23):
    c: Vertical(g0)
    c: Distance(g0) = 3
    c: Coincident(g1,g0)
    c: Horizontal(g1)
    c: Block(g0)
    c: Block(g1)
    c: Coincident(g2,g0)
    c: Vertical(g2)
    c: Distance(g2) = 0.2
    c: Coincident(g3,g2)
    c: Horizontal(g3)
    c: Block(g3)
    c: Coincident(g7,g1)
    c: Weight(g4) = 1
    c: Equal(g4,g5)
    c: Equal(g4,g6)
    c: Coincident(g7,g3)
    c: InternalAlignment(g4,g7)
    c: InternalAlignment(g5,g7)
    c: InternalAlignment(g6,g7)
    c: InternalAlignment(g8,g7)
    c: InternalAlignment(g9,g7)
    c: Block(g7)
FEATURE [Sketcher::SketchObject] Sketch028
  FullyConstrained = true
  sketch-geometry (18):
    g0: LineSegment StartX=0 StartY=3e-16 StartZ=0 EndX=0 EndY=1.7 EndZ=0
    g1: LineSegment StartX=-3.5 StartY=0 StartZ=0 EndX=-3.5 EndY=0.9 EndZ=0
    g2: Circle CenterX=-2.7 CenterY=1.7 CenterZ=0 NormalX=0 NormalY=0 NormalZ=1 AngleXU=0 Radius=1
    g3: Circle CenterX=-3.5 CenterY=1.7 CenterZ=0 NormalX=0 NormalY=0 NormalZ=1 AngleXU=0 Radius=1
    g4: Circle CenterX=-3.5 CenterY=0.9 CenterZ=0 NormalX=0 NormalY=0 NormalZ=1 AngleXU=0 Radius=1
    g5: BSplineCurve PolesCount=3 KnotsCount=2 Degree=2 IsPeriodic=0
    g6: GeomPoint X=-2.7 Y=1.7 Z=0
    g7: GeomPoint X=-3.5 Y=0.9 Z=0
    g8: LineSegment StartX=-3.5 StartY=0 StartZ=0 EndX=-3.5 EndY=-7 EndZ=0
    g9: LineSegment StartX=0 StartY=3e-16 StartZ=0 EndX=0 EndY=-7 EndZ=0
    g10: LineSegment StartX=-3.5 StartY=-7 StartZ=0 EndX=0 EndY=-7 EndZ=0
    g11: LineSegment StartX=-2.7 StartY=1.7 StartZ=0 EndX=-1.6 EndY=1.7 EndZ=0
    g12: LineSegment StartX=0 StartY=1.7 StartZ=0 EndX=0 EndY=4.5 EndZ=0
    g13: LineSegment StartX=0 StartY=4.5 StartZ=0 EndX=0 EndY=10.8 EndZ=0
    g14: LineSegment StartX=0 StartY=10.8 StartZ=0 EndX=-2 EndY=10.8 EndZ=0
    g15: LineSegment StartX=-1.6 StartY=4.7 StartZ=0 EndX=-1.6 EndY=1.7 EndZ=0
    g16: LineSegment StartX=-1.6 StartY=4.7 StartZ=0 EndX=-2 EndY=4.7 EndZ=0
    g17: LineSegment StartX=-2 StartY=4.7 StartZ=0 EndX=-2 EndY=10.8 EndZ=0
  constraints (44):
    c: Vertical(g0)
    c: Vertical(g1)
    c: Distance(g1) = 0.9
    c: Block(g0)
    c: Distance(g0) = 1.7
    c: Weight(g2) = 1
    c: Equal(g2,g3)
    c: Equal(g2,g4)
    c: Coincident(g5,g1)
    c: InternalAlignment(g2,g5)
    c: InternalAlignment(g3,g5)
    c: InternalAlignment(g4,g5)
    c: InternalAlignment(g6,g5)
    c: InternalAlignment(g7,g5)
    c: Block(g5)
    c: Coincident(g8,g1)
    c: Vertical(g8)
    c: Distance(g8) = 7
    c: Vertical(g9)
    c: Equal(g8,g9) = 7
    c: Coincident(g9,g0)
    c: Coincident(g10,g8)
    c: Coincident(g10,g9)
    c: Horizontal(g10)
    c: Coincident(g11,g5)
    c: Horizontal(g11)
    c: Coincident(g12,g0)
    c: Vertical(g12)
    c: Distance(g12) = 2.8
    c: Coincident(g13,g12)
    c: Vertical(g13)
    c: Distance(g13) = 6.3
    c: Coincident(g14,g13)
    c: Horizontal(g14)
    c: Distance(g14) = 2
    c: Vertical(g15)
    c: Distance(g15) = 3
    c: Block(g11)
    c: Coincident(g15,g11)
    c: Coincident(g16,g15)
    c: Horizontal(g16)
    c: Coincident(g17,g16)
    c: Coincident(g17,g14)
    c: Vertical(g17)
FEATURE [Part::Revolution] Revolve040  label="backCaseScrewRetainer001"
  Angle = 360
  Axis = (0,1,0)
  Base = (0,0,0)
  FaceMakerClass = Part::FaceMakerBullseye
  Placement = pos=(12.5,3,10) rot=(0,0,1;0rad)
  Solid = false
  Source = -> Face036
  Symmetric = false
FEATURE [Part::Feature] Face055
  shape: bbox 3.5 x 30.2 x 2e-07 mm, 1 faces, 0 solids (baked)
FEATURE [Part::Revolution] Revolve059  label="backCaseScrewPost"
  Angle = 360
  Axis = (0,1,0)
  Base = (0,0,0)
  FaceMakerClass = Part::FaceMakerBullseye
  Placement = pos=(12.5,4.5,10) rot=(0,0,1;0rad)
  Solid = false
  Source = -> Face055
  Symmetric = false
FEATURE [Part::Feature] Face056
  shape: bbox 3.5 x 30.2 x 2e-07 mm, 1 faces, 0 solids (baked)
FEATURE [Part::Revolution] Revolve060  label="backCaseScrewPost001"
  Angle = 360
  Axis = (0,1,0)
  Base = (0,0,0)
  FaceMakerClass = Part::FaceMakerBullseye
  Placement = pos=(12.5,4.5,62) rot=(0,0,1;0rad)
  Solid = false
  Source = -> Face056
  Symmetric = false
FEATURE [Part::Feature] Face057
  shape: bbox 3.5 x 17.8 x 2e-07 mm, 1 faces, 0 solids (baked)
FEATURE [Part::Revolution] Revolve061  label="removeToCreateScrewAndThreadedInsertHole"
  Angle = 360
  Axis = (0,1,0)
  Base = (0,0,0)
  FaceMakerClass = Part::FaceMakerBullseye
  Placement = pos=(12.5,0,10) rot=(0,0,1;0rad)
  Solid = false
  Source = -> Face057
  Symmetric = false
FEATURE [Part::Feature] Face058
  shape: bbox 3.5 x 17.8 x 2e-07 mm, 1 faces, 0 solids (baked)
FEATURE [Part::Revolution] Revolve062  label="removeToCreateScrewAndThreadedInsertHole001"
  Angle = 360
  Axis = (0,1,0)
  Base = (0,0,0)
  FaceMakerClass = Part::FaceMakerBullseye
  Placement = pos=(12.5,0,62) rot=(0,0,1;0rad)
  Solid = false
  Source = -> Face058
  Symmetric = false
FEATURE [Part::Feature] Face059
  shape: bbox 3.5 x 17.8 x 2e-07 mm, 1 faces, 0 solids (baked)
FEATURE [Part::Revolution] Revolve063  label="removeToCreateScrewAndThreadedInsertHole002"
  Angle = 360
  Axis = (0,1,0)
  Base = (0,0,0)
  FaceMakerClass = Part::FaceMakerBullseye
  Placement = pos=(89.5,0,68.5) rot=(0,0,1;0rad)
  Solid = false
  Source = -> Face059
  Symmetric = false
FEATURE [Part::Feature] Face060
  shape: bbox 3.5 x 17.8 x 2e-07 mm, 1 faces, 0 solids (baked)
FEATURE [Part::Revolution] Revolve064  label="removeToCreateScrewAndThreadedInsertHole003"
  Angle = 360
  Axis = (0,1,0)
  Base = (0,0,0)
  FaceMakerClass = Part::FaceMakerBullseye
  Placement = pos=(89.5,0,3.5) rot=(0,0,1;0rad)
  Solid = false
  Source = -> Face060
  Symmetric = false
FEATURE [Part::Feature] Face061
  shape: bbox 3.5 x 17.8 x 2e-07 mm, 1 faces, 0 solids (baked)
FEATURE [Part::Revolution] Revolve065  label="removeToCreateScrewAndThreadedInsertHole004"
  Angle = 360
  Axis = (0,1,0)
  Base = (0,0,0)
  FaceMakerClass = Part::FaceMakerBullseye
  Placement = pos=(102.5,4.7,3.5) rot=(0,0,1;0rad)
  Solid = false
  Source = -> Face061
  Symmetric = false
FEATURE [Part::Feature] Face062
  shape: bbox 3.5 x 17.8 x 2e-07 mm, 1 faces, 0 solids (baked)
FEATURE [Part::Revolution] Revolve066  label="removeToCreateScrewAndThreadedInsertHole005"
  Angle = 360
  Axis = (0,1,0)
  Base = (0,0,0)
  FaceMakerClass = Part::FaceMakerBullseye
  Placement = pos=(102.5,4.7,68.5) rot=(0,0,1;0rad)
  Solid = false
  Source = -> Face062
  Symmetric = false
FEATURE [Part::MultiFuse] Fusion047  label="makeHoles"
  Shapes = -> [Revolve066,Revolve065,Revolve064,Revolve063,Revolve062,Revolve061]
FEATURE [Part::Feature] Face063
  shape: bbox 3.6 x 3.2 x 2e-07 mm, 1 faces, 0 solids (baked)
FEATURE [Part::Revolution] Revolve067  label="moreFrontCaseScrewRetainer002"
  Angle = 360
  Axis = (0,1,0)
  Base = (0,0,0)
  FaceMakerClass = Part::FaceMakerBullseye
  Placement = pos=(102.5,4.5,68.5) rot=(0,0,1;0rad)
  Solid = false
  Source = -> Face063
  Symmetric = false
FEATURE [Part::Feature] Face064
  shape: bbox 3.6 x 3.2 x 2e-07 mm, 1 faces, 0 solids (baked)
FEATURE [Part::Revolution] Revolve068  label="moreFrontCaseScrewRetainer003"
  Angle = 360
  Axis = (0,1,0)
  Base = (0,0,0)
  FaceMakerClass = Part::FaceMakerBullseye
  Placement = pos=(102.5,4.5,3.5) rot=(0,0,1;0rad)
  Solid = false
  Source = -> Face064
  Symmetric = false
FEATURE [Part::Feature] Face065
  shape: bbox 3.5 x 17.8 x 2e-07 mm, 1 faces, 0 solids (baked)
FEATURE [Part::Revolution] Revolve069  label="removeToCreateScrewAndThreadedInsertHole006"
  Angle = 360
  Axis = (0,1,0)
  Base = (0,0,0)
  FaceMakerClass = Part::FaceMakerBullseye
  Placement = pos=(12.5,0,10) rot=(0,0,1;0rad)
  Solid = false
  Source = -> Face065
  Symmetric = false
FEATURE [Part::Feature] Face066
  shape: bbox 3.5 x 17.8 x 2e-07 mm, 1 faces, 0 solids (baked)
FEATURE [Part::Revolution] Revolve070  label="removeToCreateScrewAndThreadedInsertHole007"
  Angle = 360
  Axis = (0,1,0)
  Base = (0,0,0)
  FaceMakerClass = Part::FaceMakerBullseye
  Placement = pos=(12.5,0,62) rot=(0,0,1;0rad)
  Solid = false
  Source = -> Face066
  Symmetric = false
FEATURE [Part::Feature] Face067
  shape: bbox 3.5 x 17.8 x 2e-07 mm, 1 faces, 0 solids (baked)
FEATURE [Part::Revolution] Revolve071  label="removeToCreateScrewAndThreadedInsertHole008"
  Angle = 360
  Axis = (0,1,0)
  Base = (0,0,0)
  FaceMakerClass = Part::FaceMakerBullseye
  Placement = pos=(89.5,0,68.5) rot=(0,0,1;0rad)
  Solid = false
  Source = -> Face067
  Symmetric = false
FEATURE [Part::Feature] Face068
  shape: bbox 3.5 x 17.8 x 2e-07 mm, 1 faces, 0 solids (baked)
FEATURE [Part::Revolution] Revolve072  label="removeToCreateScrewAndThreadedInsertHole009"
  Angle = 360
  Axis = (0,1,0)
  Base = (0,0,0)
  FaceMakerClass = Part::FaceMakerBullseye
  Placement = pos=(89.5,0,3.5) rot=(0,0,1;0rad)
  Solid = false
  Source = -> Face068
  Symmetric = false
FEATURE [Part::Feature] Face069
  shape: bbox 3.5 x 17.8 x 2e-07 mm, 1 faces, 0 solids (baked)
FEATURE [Part::Feature] Face070
  shape: bbox 3.5 x 17.8 x 2e-07 mm, 1 faces, 0 solids (baked)
FEATURE [Part::Revolution] Revolve073  label="removeToCreateScrewAndThreadedInsertHole010"
  Angle = 360
  Axis = (0,1,0)
  Base = (0,0,0)
  FaceMakerClass = Part::FaceMakerBullseye
  Placement = pos=(102.5,4.7,3.5) rot=(0,0,1;0rad)
  Solid = false
  Source = -> Face069
  Symmetric = false
FEATURE [Part::Revolution] Revolve074  label="removeToCreateScrewAndThreadedInsertHole011"
  Angle = 360
  Axis = (0,1,0)
  Base = (0,0,0)
  FaceMakerClass = Part::FaceMakerBullseye
  Placement = pos=(102.5,4.7,68.5) rot=(0,0,1;0rad)
  Solid = false
  Source = -> Face070
  Symmetric = false
FEATURE [Part::MultiFuse] Fusion048  label="makeHoles001"
  Shapes = -> [Revolve074,Revolve073,Revolve072,Revolve071,Revolve070,Revolve069]
FEATURE [Part::MultiFuse] Fusion049  label="caseScrewRetainers"
  Shapes = -> [Revolve067,Revolve068,Revolve048,Revolve047,Revolve039,Revolve040]
FEATURE [Part::Cut] Cut015  label="caseScrewRetainers001"
  Base = -> Fusion049
  Tool = -> Fusion048
FEATURE [Part::MultiFuse] Fusion050  label="casePillars"
  Shapes = -> [Revolve055,Revolve054,Revolve043,Revolve046,Revolve059,Revolve060]
FEATURE [Part::Feature] Face071 .. Face076  x6 (patterned run collapsed; names and placements below)
  shape: bbox 3.5 x 17.8 x 2e-07 mm, 1 faces, 0 solids (baked)
FEATURE [Part::Revolution] Revolve075  label="removeToCreateScrewAndThreadedInsertHole012"
  Angle = 360
  Axis = (0,1,0)
  Base = (0,0,0)
  FaceMakerClass = Part::FaceMakerBullseye
  Placement = pos=(12.5,0,10) rot=(0,0,1;0rad)
  Solid = false
  Source = -> Face071
  Symmetric = false
FEATURE [Part::Revolution] Revolve076  label="removeToCreateScrewAndThreadedInsertHole013"
  Angle = 360
  Axis = (0,1,0)
  Base = (0,0,0)
  FaceMakerClass = Part::FaceMakerBullseye
  Placement = pos=(12.5,0,62) rot=(0,0,1;0rad)
  Solid = false
  Source = -> Face072
  Symmetric = false
FEATURE [Part::Revolution] Revolve077  label="removeToCreateScrewAndThreadedInsertHole014"
  Angle = 360
  Axis = (0,1,0)
  Base = (0,0,0)
  FaceMakerClass = Part::FaceMakerBullseye
  Placement = pos=(89.5,0,68.5) rot=(0,0,1;0rad)
  Solid = false
  Source = -> Face073
  Symmetric = false
FEATURE [Part::Revolution] Revolve078  label="removeToCreateScrewAndThreadedInsertHole015"
  Angle = 360
  Axis = (0,1,0)
  Base = (0,0,0)
  FaceMakerClass = Part::FaceMakerBullseye
  Placement = pos=(89.5,0,3.5) rot=(0,0,1;0rad)
  Solid = false
  Source = -> Face074
  Symmetric = false
FEATURE [Part::Revolution] Revolve079  label="removeToCreateScrewAndThreadedInsertHole016"
  Angle = 360
  Axis = (0,1,0)
  Base = (0,0,0)
  FaceMakerClass = Part::FaceMakerBullseye
  Placement = pos=(102.5,4.7,3.5) rot=(0,0,1;0rad)
  Solid = false
  Source = -> Face075
  Symmetric = false
FEATURE [Part::Revolution] Revolve080  label="removeToCreateScrewAndThreadedInsertHole017"
  Angle = 360
  Axis = (0,1,0)
  Base = (0,0,0)
  FaceMakerClass = Part::FaceMakerBullseye
  Placement = pos=(102.5,4.7,68.5) rot=(0,0,1;0rad)
  Solid = false
  Source = -> Face076
  Symmetric = false
FEATURE [Part::MultiFuse] Fusion051  label="makeHoles002"
  Shapes = -> [Revolve080,Revolve079,Revolve078,Revolve077,Revolve076,Revolve075]
FEATURE [Part::Cut] Cut016  label="caesPillars"
  Base = -> Fusion050
  Tool = -> Fusion051
FEATURE [Part::Revolution] Revolve009  label="plugHousing016"
  Angle = 360
  Axis = (0,1,0)
  Base = (0,0,0)
  FaceMakerClass = Part::FaceMakerBullseye
  Placement = pos=(0,0,36.15) rot=(0,0,1;0rad)
  Solid = false
  Source = -> Face012
  Symmetric = false
FEATURE [Part::MultiFuse] Fusion014  label="plugHousing023"
  Placement = pos=(0,0,0) rot=(0,0,1;1.5708rad)
  Shapes = -> [Revolve011,Revolve009]
FEATURE [Part::Revolution] Revolve010  label="plugHousing017"
  Angle = 360
  Axis = (0,1,0)
  Base = (0,0,0)
  FaceMakerClass = Part::FaceMakerBullseye
  Placement = pos=(0,0,36.15) rot=(0,0,1;0rad)
  Solid = false
  Source = -> Face014
  Symmetric = false
FEATURE [Part::MultiFuse] Fusion015  label="plugHousing024"
  Placement = pos=(0,0,0) rot=(0,0,1;1.5708rad)
  Shapes = -> [Revolve010,Revolve015]
FEATURE [Part::Revolution] Revolve014  label="plugHousing026"
  Angle = 360
  Axis = (0,1,0)
  Base = (0,0,0)
  FaceMakerClass = Part::FaceMakerBullseye
  Placement = pos=(0,0,36.15) rot=(0,0,1;0rad)
  Solid = false
  Source = -> Face011
  Symmetric = false
FEATURE [Part::Revolution] Revolve013  label="plugHousing025"
  Angle = 360
  Axis = (0,1,0)
  Base = (0,0,0)
  FaceMakerClass = Part::FaceMakerBullseye
  Placement = pos=(0,0,36.15) rot=(0,0,1;0rad)
  Solid = false
  Source = -> Face015
  Symmetric = false
FEATURE [Part::MultiFuse] Fusion016  label="plugHousing028"
  Placement = pos=(0,19,0) rot=(0,0,1;3.14159rad)
  Shapes = -> [Fusion014,Fusion013]
FEATURE [Part::MultiFuse] Fusion011  label="plugHousing018"
  Placement = pos=(0,0,0) rot=(0,0,1;1.5708rad)
  Shapes = -> [Revolve014,Revolve013]
FEATURE [Part::MultiFuse] Fusion012  label="plugHousing019"
  Placement = pos=(0,19,0) rot=(0,0,1;3.14159rad)
  Shapes = -> [Fusion011,Fusion015]
FEATURE [Part::MultiFuse] Fusion017  label="plugHousing029"
  Placement = pos=(122.621,0,-0.15) rot=(0,0,1;0rad)
  Shapes = -> [Fusion016,Fusion012]
FEATURE [Part::MultiFuse] Fusion052  label="casePillarRetainers"
  Shapes = -> [Extrude012,Extrude013,Extrude014,Extrude015,Extrude016,Extrude017,Extrude018,Extrude019,Box011,Box012]
FEATURE [Part::Feature] Face077
  shape: bbox 3.5 x 17.8 x 2e-07 mm, 1 faces, 0 solids (baked)
FEATURE [Part::Revolution] Revolve081  label="removeToCreateScrewAndThreadedInsertHole018"
  Angle = 360
  Axis = (0,1,0)
  Base = (0,0,0)
  FaceMakerClass = Part::FaceMakerBullseye
  Placement = pos=(62.3,30.3,19.7) rot=(0,0,1;0rad)
  Solid = false
  Source = -> Face077
  Symmetric = false
FEATURE [Part::Feature] Face078
  shape: bbox 3.5 x 17.8 x 2e-07 mm, 1 faces, 0 solids (baked)
FEATURE [Part::Revolution] Revolve082  label="removeToCreateScrewAndThreadedInsertHole019"
  Angle = 360
  Axis = (0,1,0)
  Base = (0,0,0)
  FaceMakerClass = Part::FaceMakerBullseye
  Placement = pos=(62.3,30.3,51.7) rot=(0,0,1;0rad)
  Solid = false
  Source = -> Face078
  Symmetric = false
FEATURE [Part::Feature] Face079
  shape: bbox 3.5 x 17.8 x 2e-07 mm, 1 faces, 0 solids (baked)
FEATURE [Part::Revolution] Revolve083  label="removeToCreateScrewAndThreadedInsertHole020"
  Angle = 360
  Axis = (0,1,0)
  Base = (0,0,0)
  FaceMakerClass = Part::FaceMakerBullseye
  Placement = pos=(30.3,30.3,19.7) rot=(0,0,1;0rad)
  Solid = false
  Source = -> Face079
  Symmetric = false
FEATURE [Part::Feature] Face080
  shape: bbox 3.5 x 17.8 x 2e-07 mm, 1 faces, 0 solids (baked)
FEATURE [Part::Revolution] Revolve084  label="removeToCreateScrewAndThreadedInsertHole021"
  Angle = 360
  Axis = (0,1,0)
  Base = (0,0,0)
  FaceMakerClass = Part::FaceMakerBullseye
  Placement = pos=(30.3,30.3,51.7) rot=(0,0,1;0rad)
  Solid = false
  Source = -> Face080
  Symmetric = false
FEATURE [Part::MultiFuse] Fusion053  label="createThreadedInsertHolesForFan"
  Shapes = -> [Revolve081,Revolve082,Revolve083,Revolve084]
FEATURE [Part::Cut] Cut017  label="fanScrewHousing001"
  Base = -> Fusion046
  Tool = -> Fusion053
FEATURE [Part::Feature] Face081
  shape: bbox 3.5 x 17.8 x 2e-07 mm, 1 faces, 0 solids (baked)
FEATURE [Part::Revolution] Revolve085  label="removeToCreateScrewAndThreadedInsertHole022"
  Angle = 360
  Axis = (0,1,0)
  Base = (0,0,0)
  FaceMakerClass = Part::FaceMakerBullseye
  Placement = pos=(62.3,30.3,19.7) rot=(0,0,1;0rad)
  Solid = false
  Source = -> Face081
  Symmetric = false
FEATURE [Part::Feature] Face082
  shape: bbox 3.5 x 17.8 x 2e-07 mm, 1 faces, 0 solids (baked)
FEATURE [Part::Revolution] Revolve086  label="removeToCreateScrewAndThreadedInsertHole023"
  Angle = 360
  Axis = (0,1,0)
  Base = (0,0,0)
  FaceMakerClass = Part::FaceMakerBullseye
  Placement = pos=(62.3,30.3,51.7) rot=(0,0,1;0rad)
  Solid = false
  Source = -> Face082
  Symmetric = false
FEATURE [Part::Feature] Face083
  shape: bbox 3.5 x 17.8 x 2e-07 mm, 1 faces, 0 solids (baked)
FEATURE [Part::Revolution] Revolve087  label="removeToCreateScrewAndThreadedInsertHole024"
  Angle = 360
  Axis = (0,1,0)
  Base = (0,0,0)
  FaceMakerClass = Part::FaceMakerBullseye
  Placement = pos=(30.3,30.3,19.7) rot=(0,0,1;0rad)
  Solid = false
  Source = -> Face083
  Symmetric = false
FEATURE [Part::Feature] Face084
  shape: bbox 3.5 x 17.8 x 2e-07 mm, 1 faces, 0 solids (baked)
FEATURE [Part::Revolution] Revolve088  label="removeToCreateScrewAndThreadedInsertHole025"
  Angle = 360
  Axis = (0,1,0)
  Base = (0,0,0)
  FaceMakerClass = Part::FaceMakerBullseye
  Placement = pos=(30.3,30.3,51.7) rot=(0,0,1;0rad)
  Solid = false
  Source = -> Face084
  Symmetric = false
FEATURE [Part::MultiFuse] Fusion054  label="createThreadedInsertHolesForFan001"
  Shapes = -> [Revolve085,Revolve086,Revolve087,Revolve088]
FEATURE [Part::Cut] Cut018  label="top007"
  Base = -> Fusion040
  Tool = -> Fusion054
FEATURE [Sketcher::SketchObject] Sketch029
  FullyConstrained = false
  Placement = pos=(0,0,0) rot=(1,0,0;1.5708rad)
  sketch-geometry (24):
    g0: ArcOfCircle CenterX=-4 CenterY=-10.5 CenterZ=0 NormalX=0 NormalY=0 NormalZ=1 AngleXU=0 Radius=1.5 StartAngle=6e-16 EndAngle=3.14159
    g1: ArcOfCircle CenterX=-34.2 CenterY=-10.5 CenterZ=0 NormalX=0 NormalY=0 NormalZ=1 AngleXU=0 Radius=1.5 StartAngle=0 EndAngle=3.14159
    g2: ArcOfCircle CenterX=-34.2 CenterY=-27.7 CenterZ=0 NormalX=0 NormalY=0 NormalZ=1 AngleXU=0 Radius=1.5 StartAngle=3.14159 EndAngle=6.28319
    g3: ArcOfCircle CenterX=-4 CenterY=-27.7 CenterZ=0 NormalX=0 NormalY=0 NormalZ=1 AngleXU=0 Radius=1.5 StartAngle=3.1416 EndAngle=6.28319
    g4: ArcOfCircle CenterX=-10 CenterY=-4.3 CenterZ=0 NormalX=0 NormalY=0 NormalZ=1 AngleXU=0 Radius=1.5 StartAngle=2e-16 EndAngle=3.14159
    g5: ArcOfCircle CenterX=-16.1 CenterY=-1.8 CenterZ=0 NormalX=0 NormalY=0 NormalZ=1 AngleXU=0 Radius=1.5 StartAngle=5e-16 EndAngle=3.14159
    g6: ArcOfCircle CenterX=-22.1 CenterY=-1.8 CenterZ=0 NormalX=0 NormalY=0 NormalZ=1 AngleXU=0 Radius=1.5 StartAngle=5e-16 EndAngle=3.14159
    g7: ArcOfCircle CenterX=-28.2 CenterY=-4.3 CenterZ=0 NormalX=0 NormalY=0 NormalZ=1 AngleXU=0 Radius=1.5 StartAngle=2e-16 EndAngle=3.14159
    g8: ArcOfCircle CenterX=-10 CenterY=-33.9 CenterZ=0 NormalX=0 NormalY=0 NormalZ=1 AngleXU=0 Radius=1.5 StartAngle=3.14159 EndAngle=6.28319
    g9: ArcOfCircle CenterX=-16.1 CenterY=-36.4 CenterZ=0 NormalX=0 NormalY=0 NormalZ=1 AngleXU=0 Radius=1.5 StartAngle=3.14159 EndAngle=6.28319
    g10: ArcOfCircle CenterX=-22.1 CenterY=-36.4 CenterZ=0 NormalX=0 NormalY=0 NormalZ=1 AngleXU=0 Radius=1.5 StartAngle=3.14159 EndAngle=6.28319
    g11: ArcOfCircle CenterX=-28.2 CenterY=-33.9 CenterZ=0 NormalX=0 NormalY=0 NormalZ=1 AngleXU=0 Radius=1.5 StartAngle=3.14159 EndAngle=6.28319
    g12: LineSegment StartX=-35.7 StartY=-10.5 StartZ=0 EndX=-35.7 EndY=-27.7 EndZ=0
    g13: LineSegment StartX=-32.7 StartY=-10.5 StartZ=0 EndX=-32.7 EndY=-27.7 EndZ=0
    g14: LineSegment StartX=-29.7 StartY=-33.9 StartZ=0 EndX=-29.7 EndY=-4.3 EndZ=0
    g15: LineSegment StartX=-26.7 StartY=-33.9 StartZ=0 EndX=-26.7 EndY=-4.3 EndZ=0
    g16: LineSegment StartX=-2.5 StartY=-10.5 StartZ=0 EndX=-2.5 EndY=-27.7 EndZ=0
    g17: LineSegment StartX=-8.5 StartY=-4.3 StartZ=0 EndX=-8.5 EndY=-33.9 EndZ=0
    g18: LineSegment StartX=-5.5 StartY=-10.5 StartZ=0 EndX=-5.5 EndY=-27.7 EndZ=0
    g19: LineSegment StartX=-11.5 StartY=-4.3 StartZ=0 EndX=-11.5 EndY=-33.9 EndZ=0
    g20: LineSegment StartX=-14.6 StartY=-1.8 StartZ=0 EndX=-14.6 EndY=-36.4 EndZ=0
    g21: LineSegment StartX=-17.6 StartY=-1.8 StartZ=0 EndX=-17.6 EndY=-36.4 EndZ=0
    g22: LineSegment StartX=-20.6 StartY=-36.4 StartZ=0 EndX=-20.6 EndY=-1.8 EndZ=0
    g23: LineSegment StartX=-23.6 StartY=-1.8 StartZ=0 EndX=-23.6 EndY=-36.4 EndZ=0
  constraints (48):
    c: Block(g0)
    c: Block(g1)
    c: Block(g2)
    c: Block(g3)
    c: Block(g4)
    c: Block(g5)
    c: Block(g6)
    c: Block(g7)
    c: Block(g8)
    c: Block(g9)
    c: Block(g10)
    c: Block(g11)
    c: Coincident(g12,g1)
    c: Coincident(g12,g2)
    c: Vertical(g12)
    c: Coincident(g13,g1)
    c: Coincident(g13,g2)
    c: Vertical(g13)
    c: Coincident(g14,g11)
    c: Coincident(g14,g7)
    c: Vertical(g14)
    c: Coincident(g15,g11)
    c: Coincident(g15,g7)
    c: Vertical(g15)
    c: Coincident(g16,g0)
    c: Coincident(g16,g3)
    c: Vertical(g16)
    c: Coincident(g17,g4)
    c: Coincident(g17,g8)
    c: Vertical(g17)
    c: Coincident(g18,g0)
    c: Coincident(g18,g3)
    c: Vertical(g18)
    c: Coincident(g19,g4)
    c: Coincident(g19,g8)
    c: Vertical(g19)
    c: Coincident(g20,g5)
    c: Coincident(g20,g9)
    c: Vertical(g20)
    c: Coincident(g21,g5)
    c: Coincident(g21,g9)
    c: Vertical(g21)
    c: Coincident(g22,g10)
    c: Coincident(g22,g6)
    c: Vertical(g22)
    c: Coincident(g23,g6)
    c: Coincident(g23,g10)
    c: Vertical(g23)
FEATURE [Part::Extrusion] Extrude020  label="removeToCreateFanGrillHoles"
  Base = -> Sketch029
  Dir = (0,-1,6e-16)
  DirMode = 2
  FaceMakerClass = Part::FaceMakerBullseye
  LengthFwd = 10
  LengthRev = 0
  Placement = pos=(65.4,44,54.82) rot=(0,0,1;0rad)
  Solid = true
  Symmetric = false
FEATURE [Part::MultiFuse] Fusion055  label="top008"
  Shapes = -> [Cut017,Cut018]
FEATURE [Part::Cut] Cut019  label="top009"
  Base = -> Fusion055
  Tool = -> Extrude020
FEATURE [App::MeasureDistance] Distance003  label="Distance: 71.95 mm"
  Distance = 71.9513
  P1 = (117,38,72)
  P2 = (117,38,0.0487319)
FEATURE [Sketcher::SketchObject] Sketch030
  FullyConstrained = true
  Placement = pos=(117,19,0) rot=(0.57735,0.57735,0.57735;2.0944rad)
  sketch-geometry (48):
    g0: LineSegment StartX=-49.19 StartY=69.25 StartZ=0 EndX=-49.19 EndY=66.25 EndZ=0
    g1: LineSegment StartX=-49.19 StartY=63.5 StartZ=0 EndX=-49.19 EndY=60.5 EndZ=0
    g2: LineSegment StartX=-49.19 StartY=57.75 StartZ=0 EndX=-49.19 EndY=54.75 EndZ=0
    g3: LineSegment StartX=-49.19 StartY=52 StartZ=0 EndX=-49.19 EndY=49 EndZ=0
    g4: LineSegment StartX=-49.19 StartY=46.25 StartZ=0 EndX=-49.19 EndY=43.25 EndZ=0
    g5: LineSegment StartX=-49.19 StartY=40.5 StartZ=0 EndX=-49.19 EndY=37.5 EndZ=0
    g6: LineSegment StartX=-49.19 StartY=34.5 StartZ=0 EndX=-49.19 EndY=31.5 EndZ=0
    g7: LineSegment StartX=-49.19 StartY=28.75 StartZ=0 EndX=-49.19 EndY=25.75 EndZ=0
    g8: LineSegment StartX=-49.19 StartY=23 StartZ=0 EndX=-49.19 EndY=20 EndZ=0
    g9: LineSegment StartX=-49.19 StartY=17.25 StartZ=0 EndX=-49.19 EndY=14.25 EndZ=0
    g10: LineSegment StartX=-49.19 StartY=11.5 StartZ=0 EndX=-49.19 EndY=8.5 EndZ=0
    g11: LineSegment StartX=-49.19 StartY=5.75 StartZ=0 EndX=-49.19 EndY=2.75 EndZ=0
    g12: ArcOfCircle CenterX=-1.5 CenterY=67.75 CenterZ=0 NormalX=0 NormalY=0 NormalZ=1 AngleXU=0 Radius=1.5 StartAngle=4.71239 EndAngle=7.85398
    g13: ArcOfCircle CenterX=-1.5 CenterY=62 CenterZ=0 NormalX=0 NormalY=0 NormalZ=1 AngleXU=0 Radius=1.5 StartAngle=4.71239 EndAngle=7.85398
    g14: ArcOfCircle CenterX=-1.5 CenterY=56.25 CenterZ=0 NormalX=0 NormalY=0 NormalZ=1 AngleXU=0 Radius=1.5 StartAngle=4.71239 EndAngle=7.85398
    g15: ArcOfCircle CenterX=-11.49 CenterY=50.5 CenterZ=0 NormalX=0 NormalY=0 NormalZ=1 AngleXU=0 Radius=1.5 StartAngle=4.71239 EndAngle=7.85398
    g16: ArcOfCircle CenterX=-16.28 CenterY=44.75 CenterZ=0 NormalX=0 NormalY=0 NormalZ=1 AngleXU=0 Radius=1.5 StartAngle=4.71239 EndAngle=7.85398
    g17: ArcOfCircle CenterX=-18.2337 CenterY=39 CenterZ=0 NormalX=0 NormalY=0 NormalZ=1 AngleXU=0 Radius=1.5 StartAngle=4.71485 EndAngle=7.85398
    g18: ArcOfCircle CenterX=-16.2837 CenterY=27.25 CenterZ=0 NormalX=0 NormalY=0 NormalZ=1 AngleXU=0 Radius=1.5 StartAngle=4.71485 EndAngle=7.85398
    g19: ArcOfCircle CenterX=-18.2337 CenterY=33 CenterZ=0 NormalX=0 NormalY=0 NormalZ=1 AngleXU=0 Radius=1.5 StartAngle=4.71485 EndAngle=7.85398
    g20: ArcOfCircle CenterX=-11.49 CenterY=21.5 CenterZ=0 NormalX=0 NormalY=0 NormalZ=1 AngleXU=0 Radius=1.5 StartAngle=4.71239 EndAngle=7.85398
    g21: ArcOfCircle CenterX=-1.5 CenterY=4.25 CenterZ=0 NormalX=0 NormalY=0 NormalZ=1 AngleXU=0 Radius=1.5 StartAngle=4.71239 EndAngle=7.85398
    g22: ArcOfCircle CenterX=-1.5 CenterY=10 CenterZ=0 NormalX=0 NormalY=0 NormalZ=1 AngleXU=0 Radius=1.5 StartAngle=4.71239 EndAngle=7.85398
    g23: ArcOfCircle CenterX=-1.5 CenterY=15.75 CenterZ=0 NormalX=0 NormalY=0 NormalZ=1 AngleXU=0 Radius=1.5 StartAngle=4.71239 EndAngle=7.85398
    g24: LineSegment StartX=-49.19 StartY=69.25 StartZ=0 EndX=-1.5 EndY=69.25 EndZ=0
    g25: LineSegment StartX=-49.19 StartY=66.25 StartZ=0 EndX=-1.5 EndY=66.25 EndZ=0
    g26: LineSegment StartX=-49.19 StartY=63.5 StartZ=0 EndX=-1.5 EndY=63.5 EndZ=0
    g27: LineSegment StartX=-49.19 StartY=60.5 StartZ=0 EndX=-1.5 EndY=60.5 EndZ=0
    g28: LineSegment StartX=-49.19 StartY=57.75 StartZ=0 EndX=-1.5 EndY=57.75 EndZ=0
    g29: LineSegment StartX=-49.19 StartY=54.75 StartZ=0 EndX=-1.5 EndY=54.75 EndZ=0
    g30: LineSegment StartX=-49.19 StartY=52 StartZ=0 EndX=-11.49 EndY=52 EndZ=0
    g31: LineSegment StartX=-49.19 StartY=49 StartZ=0 EndX=-11.49 EndY=49 EndZ=0
    g32: LineSegment StartX=-49.19 StartY=46.25 StartZ=0 EndX=-16.28 EndY=46.25 EndZ=0
    g33: LineSegment StartX=-49.19 StartY=43.25 StartZ=0 EndX=-16.28 EndY=43.25 EndZ=0
    g34: LineSegment StartX=-49.19 StartY=40.5 StartZ=0 EndX=-18.2337 EndY=40.5 EndZ=0
    g35: LineSegment StartX=-49.19 StartY=37.5 StartZ=0 EndX=-18.23 EndY=37.5 EndZ=0
    g36: LineSegment StartX=-49.19 StartY=34.5 StartZ=0 EndX=-18.2337 EndY=34.5 EndZ=0
    g37: LineSegment StartX=-49.19 StartY=31.5 StartZ=0 EndX=-18.23 EndY=31.5 EndZ=0
    g38: LineSegment StartX=-49.19 StartY=28.75 StartZ=0 EndX=-16.2837 EndY=28.75 EndZ=0
    g39: LineSegment StartX=-49.19 StartY=25.75 StartZ=0 EndX=-16.28 EndY=25.75 EndZ=0
    g40: LineSegment StartX=-49.19 StartY=23 StartZ=0 EndX=-11.49 EndY=23 EndZ=0
    g41: LineSegment StartX=-49.19 StartY=20 StartZ=0 EndX=-11.49 EndY=20 EndZ=0
    g42: LineSegment StartX=-49.19 StartY=17.25 StartZ=0 EndX=-1.5 EndY=17.25 EndZ=0
    g43: LineSegment StartX=-49.19 StartY=14.25 StartZ=0 EndX=-1.5 EndY=14.25 EndZ=0
    g44: LineSegment StartX=-49.19 StartY=11.5 StartZ=0 EndX=-1.5 EndY=11.5 EndZ=0
    g45: LineSegment StartX=-49.19 StartY=8.5 StartZ=0 EndX=-1.5 EndY=8.5 EndZ=0
    g46: LineSegment StartX=-49.19 StartY=5.75 StartZ=0 EndX=-1.5 EndY=5.75 EndZ=0
    g47: LineSegment StartX=-49.19 StartY=2.75 StartZ=0 EndX=-1.5 EndY=2.75 EndZ=0
  constraints (120):
    c: Vertical(g0)
    c: Distance(g0) = 3
    c: Block(g0)
    c: Vertical(g1)
    c: Distance(g1) = 3
    c: Vertical(g2)
    c: Equal(g0,g2) = 3
    c: Block(g2)
    c: Vertical(g3)
    c: Equal(g1,g3) = 3
    c: Vertical(g4)
    c: Equal(g0,g4) = 3
    c: Block(g4)
    c: Vertical(g5)
    c: Equal(g1,g5) = 3
    c: Vertical(g6)
    c: Equal(g0,g6) = 3
    c: Block(g6)
    c: Vertical(g7)
    c: Equal(g1,g7) = 3
    c: Vertical(g8)
    c: Equal(g0,g8) = 3
    c: Block(g8)
    c: Vertical(g9)
    c: Equal(g1,g9) = 3
    c: Vertical(g10)
    c: Equal(g0,g10) = 3
    c: Block(g10)
    c: Vertical(g11)
    c: Equal(g1,g11) = 3
    c: Block(g12)
    c: Block(g13)
    c: Block(g14)
    c: Block(g15)
    c: Block(g16)
    c: Block(g17)
    c: Block(g18)
    c: Block(g19)
    c: Block(g20)
    c: Block(g21)
    c: Block(g22)
    c: Block(g23)
    c: Block(g11)
    c: Block(g9)
    c: Block(g7)
    c: Block(g5)
    c: Block(g3)
    c: Block(g1)
    c: Coincident(g24,g0)
    c: Coincident(g24,g12)
    c: Horizontal(g24)
    c: Coincident(g25,g0)
    c: Coincident(g25,g12)
    c: Horizontal(g25)
    c: Coincident(g26,g1)
    c: Coincident(g26,g13)
    c: Horizontal(g26)
    c: Coincident(g27,g1)
    c: Coincident(g27,g13)
    c: Horizontal(g27)
    c: Coincident(g28,g2)
    c: Coincident(g28,g14)
    c: Horizontal(g28)
    c: Coincident(g29,g2)
    c: Coincident(g29,g14)
    c: Horizontal(g29)
    c: Coincident(g30,g3)
    c: Coincident(g30,g15)
    c: Horizontal(g30)
    c: Coincident(g31,g3)
    c: Coincident(g31,g15)
    c: Horizontal(g31)
    c: Coincident(g32,g4)
    c: Coincident(g32,g16)
    c: Horizontal(g32)
    c: Coincident(g33,g4)
    c: Coincident(g33,g16)
    c: Horizontal(g33)
    c: Coincident(g34,g5)
    c: Coincident(g34,g17)
    c: Horizontal(g34)
    c: Coincident(g35,g5)
    c: Coincident(g35,g17)
    c: Horizontal(g35)
    c: Coincident(g36,g6)
    c: Coincident(g36,g19)
    c: Horizontal(g36)
    c: Coincident(g37,g6)
    c: Coincident(g37,g19)
    c: Horizontal(g37)
    c: Coincident(g38,g7)
    c: Coincident(g38,g18)
    c: Horizontal(g38)
    c: Coincident(g39,g7)
    c: Coincident(g39,g18)
    c: Horizontal(g39)
    c: Coincident(g40,g8)
    c: Coincident(g40,g20)
    c: Horizontal(g40)
    c: Coincident(g41,g8)
    c: Coincident(g41,g20)
    c: Horizontal(g41)
    c: Coincident(g42,g9)
    c: Coincident(g42,g23)
    c: Horizontal(g42)
    c: Coincident(g43,g9)
    c: Coincident(g43,g23)
    c: Horizontal(g43)
    c: Coincident(g44,g10)
    c: Coincident(g44,g22)
    c: Horizontal(g44)
    c: Coincident(g45,g10)
    c: Coincident(g45,g22)
    c: Horizontal(g45)
    c: Coincident(g46,g11)
    c: Coincident(g46,g21)
    c: Horizontal(g46)
    c: Coincident(g47,g11)
    c: Coincident(g47,g21)
    c: Horizontal(g47)
FEATURE [Sketcher::SketchObject] Sketch031
  FullyConstrained = true
  Placement = pos=(117,19,0) rot=(0.57735,0.57735,0.57735;2.0944rad)
  sketch-geometry (24):
    g0: ArcOfCircle CenterX=-49.19 CenterY=67.75 CenterZ=0 NormalX=0 NormalY=0 NormalZ=1 AngleXU=0 Radius=1.5 StartAngle=1.5708 EndAngle=4.71239
    g1: ArcOfCircle CenterX=-49.19 CenterY=62 CenterZ=0 NormalX=0 NormalY=0 NormalZ=1 AngleXU=0 Radius=1.5 StartAngle=1.5708 EndAngle=4.71239
    g2: ArcOfCircle CenterX=-49.19 CenterY=56.25 CenterZ=0 NormalX=0 NormalY=0 NormalZ=1 AngleXU=0 Radius=1.5 StartAngle=1.5708 EndAngle=4.71239
    g3: ArcOfCircle CenterX=-49.19 CenterY=50.5 CenterZ=0 NormalX=0 NormalY=0 NormalZ=1 AngleXU=0 Radius=1.5 StartAngle=1.5708 EndAngle=4.71239
    g4: ArcOfCircle CenterX=-49.19 CenterY=44.75 CenterZ=0 NormalX=0 NormalY=0 NormalZ=1 AngleXU=0 Radius=1.5 StartAngle=1.5708 EndAngle=4.71239
    g5: ArcOfCircle CenterX=-49.19 CenterY=39 CenterZ=0 NormalX=0 NormalY=0 NormalZ=1 AngleXU=0 Radius=1.5 StartAngle=1.5708 EndAngle=4.71239
    g6: ArcOfCircle CenterX=-49.19 CenterY=33 CenterZ=0 NormalX=0 NormalY=0 NormalZ=1 AngleXU=0 Radius=1.5 StartAngle=1.5708 EndAngle=4.71239
    g7: ArcOfCircle CenterX=-49.19 CenterY=27.25 CenterZ=0 NormalX=0 NormalY=0 NormalZ=1 AngleXU=0 Radius=1.5 StartAngle=1.5708 EndAngle=4.71239
    g8: ArcOfCircle CenterX=-49.19 CenterY=21.5 CenterZ=0 NormalX=0 NormalY=0 NormalZ=1 AngleXU=0 Radius=1.5 StartAngle=1.5708 EndAngle=4.71239
    g9: ArcOfCircle CenterX=-49.19 CenterY=15.75 CenterZ=0 NormalX=0 NormalY=0 NormalZ=1 AngleXU=0 Radius=1.5 StartAngle=1.5708 EndAngle=4.71239
    g10: ArcOfCircle CenterX=-49.19 CenterY=10 CenterZ=0 NormalX=0 NormalY=0 NormalZ=1 AngleXU=0 Radius=1.5 StartAngle=1.5708 EndAngle=4.71239
    g11: ArcOfCircle CenterX=-49.19 CenterY=4.25 CenterZ=0 NormalX=0 NormalY=0 NormalZ=1 AngleXU=0 Radius=1.5 StartAngle=1.5708 EndAngle=4.71239
    g12: LineSegment StartX=-49.19 StartY=69.25 StartZ=0 EndX=-49.19 EndY=66.25 EndZ=0
    g13: LineSegment StartX=-49.19 StartY=63.5 StartZ=0 EndX=-49.19 EndY=60.5 EndZ=0
    g14: LineSegment StartX=-49.19 StartY=57.75 StartZ=0 EndX=-49.19 EndY=54.75 EndZ=0
    g15: LineSegment StartX=-49.19 StartY=52 StartZ=0 EndX=-49.19 EndY=49 EndZ=0
    g16: LineSegment StartX=-49.19 StartY=46.25 StartZ=0 EndX=-49.19 EndY=43.25 EndZ=0
    g17: LineSegment StartX=-49.19 StartY=40.5 StartZ=0 EndX=-49.19 EndY=37.5 EndZ=0
    g18: LineSegment StartX=-49.19 StartY=34.5 StartZ=0 EndX=-49.19 EndY=31.5 EndZ=0
    g19: LineSegment StartX=-49.19 StartY=28.75 StartZ=0 EndX=-49.19 EndY=25.75 EndZ=0
    g20: LineSegment StartX=-49.19 StartY=23 StartZ=0 EndX=-49.19 EndY=20 EndZ=0
    g21: LineSegment StartX=-49.19 StartY=17.25 StartZ=0 EndX=-49.19 EndY=14.25 EndZ=0
    g22: LineSegment StartX=-49.19 StartY=11.5 StartZ=0 EndX=-49.19 EndY=8.5 EndZ=0
    g23: LineSegment StartX=-49.19 StartY=5.75 StartZ=0 EndX=-49.19 EndY=2.75 EndZ=0
  constraints (48):
    c: Block(g0)
    c: Block(g1)
    c: Block(g2)
    c: Block(g3)
    c: Block(g4)
    c: Block(g5)
    c: Block(g6)
    c: Block(g7)
    c: Block(g8)
    c: Block(g9)
    c: Block(g10)
    c: Block(g11)
    c: Coincident(g12,g0)
    c: Coincident(g12,g0)
    c: Vertical(g12)
    c: Vertical(g13)
    c: Coincident(g13,g1)
    c: Vertical(g14)
    c: Coincident(g14,g2)
    c: Vertical(g15)
    c: Coincident(g15,g3)
    c: Vertical(g16)
    c: Coincident(g16,g4)
    c: Vertical(g17)
    c: Coincident(g17,g5)
    c: Vertical(g18)
    c: Coincident(g18,g6)
    c: Vertical(g19)
    c: Coincident(g19,g7)
    c: Vertical(g20)
    c: Coincident(g20,g8)
    c: Vertical(g21)
    c: Coincident(g21,g9)
    c: Vertical(g22)
    c: Coincident(g22,g10)
    c: Vertical(g23)
    c: Coincident(g23,g11)
    c: Block(g23)
    c: Block(g22)
    c: Block(g21)
    c: Block(g20)
    c: Block(g13)
    c: Block(g14)
    c: Block(g15)
    c: Block(g16)
    c: Block(g17)
    c: Block(g18)
    c: Block(g19)
FEATURE [Part::Extrusion] Extrude022
  Base = -> Sketch030
  Dir = (1,-2e-16,2e-16)
  DirMode = 2
  FaceMakerClass = Part::FaceMakerBullseye
  LengthFwd = 19
  LengthRev = 0
  Placement = pos=(-19,0,0) rot=(0,0,1;0rad)
  Solid = true
  Symmetric = false
FEATURE [Part::Fillet] Fillet022
  Base = -> Extrude022
  Edges = 24 edges r=1.49: [Edge6,Edge11,Edge18,Edge23,Edge30,Edge35,Edge42,Edge47,Edge54,Edge59,Edge66,Edge71,Edge78,Edge83,Edge90,Edge95,Edge102,Edge107,Edge114,Edge119,Edge126,Edge131,Edge138,Edge143]
FEATURE [Part::Cut] Cut020  label="top010"
  Base = -> Cut019
  Tool = -> Fillet022
FEATURE [Sketcher::SketchObject] Sketch032
  FullyConstrained = true
  Placement = pos=(117,19,0) rot=(0.57735,0.57735,0.57735;2.0944rad)
  sketch-geometry (48):
    g0: LineSegment StartX=-49.19 StartY=69.25 StartZ=0 EndX=-49.19 EndY=66.25 EndZ=0
    g1: LineSegment StartX=-49.19 StartY=63.5 StartZ=0 EndX=-49.19 EndY=60.5 EndZ=0
    g2: LineSegment StartX=-49.19 StartY=57.75 StartZ=0 EndX=-49.19 EndY=54.75 EndZ=0
    g3: LineSegment StartX=-49.19 StartY=52 StartZ=0 EndX=-49.19 EndY=49 EndZ=0
    g4: LineSegment StartX=-49.19 StartY=46.25 StartZ=0 EndX=-49.19 EndY=43.25 EndZ=0
    g5: LineSegment StartX=-49.19 StartY=40.5 StartZ=0 EndX=-49.19 EndY=37.5 EndZ=0
    g6: LineSegment StartX=-49.19 StartY=34.5 StartZ=0 EndX=-49.19 EndY=31.5 EndZ=0
    g7: LineSegment StartX=-49.19 StartY=28.75 StartZ=0 EndX=-49.19 EndY=25.75 EndZ=0
    g8: LineSegment StartX=-49.19 StartY=23 StartZ=0 EndX=-49.19 EndY=20 EndZ=0
    g9: LineSegment StartX=-49.19 StartY=17.25 StartZ=0 EndX=-49.19 EndY=14.25 EndZ=0
    g10: LineSegment StartX=-49.19 StartY=11.5 StartZ=0 EndX=-49.19 EndY=8.5 EndZ=0
    g11: LineSegment StartX=-49.19 StartY=5.75 StartZ=0 EndX=-49.19 EndY=2.75 EndZ=0
    g12: ArcOfCircle CenterX=-1.5 CenterY=67.75 CenterZ=0 NormalX=0 NormalY=0 NormalZ=1 AngleXU=0 Radius=1.5 StartAngle=4.71239 EndAngle=7.85398
    g13: ArcOfCircle CenterX=-1.5 CenterY=62 CenterZ=0 NormalX=0 NormalY=0 NormalZ=1 AngleXU=0 Radius=1.5 StartAngle=4.71239 EndAngle=7.85398
    g14: ArcOfCircle CenterX=-1.5 CenterY=56.25 CenterZ=0 NormalX=0 NormalY=0 NormalZ=1 AngleXU=0 Radius=1.5 StartAngle=4.71239 EndAngle=7.85398
    g15: ArcOfCircle CenterX=-11.49 CenterY=50.5 CenterZ=0 NormalX=0 NormalY=0 NormalZ=1 AngleXU=0 Radius=1.5 StartAngle=4.71239 EndAngle=7.85398
    g16: ArcOfCircle CenterX=-16.28 CenterY=44.75 CenterZ=0 NormalX=0 NormalY=0 NormalZ=1 AngleXU=0 Radius=1.5 StartAngle=4.71239 EndAngle=7.85398
    g17: ArcOfCircle CenterX=-18.2337 CenterY=39 CenterZ=0 NormalX=0 NormalY=0 NormalZ=1 AngleXU=0 Radius=1.5 StartAngle=4.71485 EndAngle=7.85398
    g18: ArcOfCircle CenterX=-16.2837 CenterY=27.25 CenterZ=0 NormalX=0 NormalY=0 NormalZ=1 AngleXU=0 Radius=1.5 StartAngle=4.71485 EndAngle=7.85398
    g19: ArcOfCircle CenterX=-18.2337 CenterY=33 CenterZ=0 NormalX=0 NormalY=0 NormalZ=1 AngleXU=0 Radius=1.5 StartAngle=4.71485 EndAngle=7.85398
    g20: ArcOfCircle CenterX=-11.49 CenterY=21.5 CenterZ=0 NormalX=0 NormalY=0 NormalZ=1 AngleXU=0 Radius=1.5 StartAngle=4.71239 EndAngle=7.85398
    g21: ArcOfCircle CenterX=-1.5 CenterY=4.25 CenterZ=0 NormalX=0 NormalY=0 NormalZ=1 AngleXU=0 Radius=1.5 StartAngle=4.71239 EndAngle=7.85398
    g22: ArcOfCircle CenterX=-1.5 CenterY=10 CenterZ=0 NormalX=0 NormalY=0 NormalZ=1 AngleXU=0 Radius=1.5 StartAngle=4.71239 EndAngle=7.85398
    g23: ArcOfCircle CenterX=-1.5 CenterY=15.75 CenterZ=0 NormalX=0 NormalY=0 NormalZ=1 AngleXU=0 Radius=1.5 StartAngle=4.71239 EndAngle=7.85398
    g24: LineSegment StartX=-49.19 StartY=69.25 StartZ=0 EndX=-1.5 EndY=69.25 EndZ=0
    g25: LineSegment StartX=-49.19 StartY=66.25 StartZ=0 EndX=-1.5 EndY=66.25 EndZ=0
    g26: LineSegment StartX=-49.19 StartY=63.5 StartZ=0 EndX=-1.5 EndY=63.5 EndZ=0
    g27: LineSegment StartX=-49.19 StartY=60.5 StartZ=0 EndX=-1.5 EndY=60.5 EndZ=0
    g28: LineSegment StartX=-49.19 StartY=57.75 StartZ=0 EndX=-1.5 EndY=57.75 EndZ=0
    g29: LineSegment StartX=-49.19 StartY=54.75 StartZ=0 EndX=-1.5 EndY=54.75 EndZ=0
    g30: LineSegment StartX=-49.19 StartY=52 StartZ=0 EndX=-11.49 EndY=52 EndZ=0
    g31: LineSegment StartX=-49.19 StartY=49 StartZ=0 EndX=-11.49 EndY=49 EndZ=0
    g32: LineSegment StartX=-49.19 StartY=46.25 StartZ=0 EndX=-16.28 EndY=46.25 EndZ=0
    g33: LineSegment StartX=-49.19 StartY=43.25 StartZ=0 EndX=-16.28 EndY=43.25 EndZ=0
    g34: LineSegment StartX=-49.19 StartY=40.5 StartZ=0 EndX=-18.2337 EndY=40.5 EndZ=0
    g35: LineSegment StartX=-49.19 StartY=37.5 StartZ=0 EndX=-18.23 EndY=37.5 EndZ=0
    g36: LineSegment StartX=-49.19 StartY=34.5 StartZ=0 EndX=-18.2337 EndY=34.5 EndZ=0
    g37: LineSegment StartX=-49.19 StartY=31.5 StartZ=0 EndX=-18.23 EndY=31.5 EndZ=0
    g38: LineSegment StartX=-49.19 StartY=28.75 StartZ=0 EndX=-16.2837 EndY=28.75 EndZ=0
    g39: LineSegment StartX=-49.19 StartY=25.75 StartZ=0 EndX=-16.28 EndY=25.75 EndZ=0
    g40: LineSegment StartX=-49.19 StartY=23 StartZ=0 EndX=-11.49 EndY=23 EndZ=0
    g41: LineSegment StartX=-49.19 StartY=20 StartZ=0 EndX=-11.49 EndY=20 EndZ=0
    g42: LineSegment StartX=-49.19 StartY=17.25 StartZ=0 EndX=-1.5 EndY=17.25 EndZ=0
    g43: LineSegment StartX=-49.19 StartY=14.25 StartZ=0 EndX=-1.5 EndY=14.25 EndZ=0
    g44: LineSegment StartX=-49.19 StartY=11.5 StartZ=0 EndX=-1.5 EndY=11.5 EndZ=0
    g45: LineSegment StartX=-49.19 StartY=8.5 StartZ=0 EndX=-1.5 EndY=8.5 EndZ=0
    g46: LineSegment StartX=-49.19 StartY=5.75 StartZ=0 EndX=-1.5 EndY=5.75 EndZ=0
    g47: LineSegment StartX=-49.19 StartY=2.75 StartZ=0 EndX=-1.5 EndY=2.75 EndZ=0
  constraints (120):
    c: Vertical(g0)
    c: Distance(g0) = 3
    c: Block(g0)
    c: Vertical(g1)
    c: Distance(g1) = 3
    c: Vertical(g2)
    c: Equal(g0,g2) = 3
    c: Block(g2)
    c: Vertical(g3)
    c: Equal(g1,g3) = 3
    c: Vertical(g4)
    c: Equal(g0,g4) = 3
    c: Block(g4)
    c: Vertical(g5)
    c: Equal(g1,g5) = 3
    c: Vertical(g6)
    c: Equal(g0,g6) = 3
    c: Block(g6)
    c: Vertical(g7)
    c: Equal(g1,g7) = 3
    c: Vertical(g8)
    c: Equal(g0,g8) = 3
    c: Block(g8)
    c: Vertical(g9)
    c: Equal(g1,g9) = 3
    c: Vertical(g10)
    c: Equal(g0,g10) = 3
    c: Block(g10)
    c: Vertical(g11)
    c: Equal(g1,g11) = 3
    c: Block(g12)
    c: Block(g13)
    c: Block(g14)
    c: Block(g15)
    c: Block(g16)
    c: Block(g17)
    c: Block(g18)
    c: Block(g19)
    c: Block(g20)
    c: Block(g21)
    c: Block(g22)
    c: Block(g23)
    c: Block(g11)
    c: Block(g9)
    c: Block(g7)
    c: Block(g5)
    c: Block(g3)
    c: Block(g1)
    c: Coincident(g24,g0)
    c: Coincident(g24,g12)
    c: Horizontal(g24)
    c: Coincident(g25,g0)
    c: Coincident(g25,g12)
    c: Horizontal(g25)
    c: Coincident(g26,g1)
    c: Coincident(g26,g13)
    c: Horizontal(g26)
    c: Coincident(g27,g1)
    c: Coincident(g27,g13)
    c: Horizontal(g27)
    c: Coincident(g28,g2)
    c: Coincident(g28,g14)
    c: Horizontal(g28)
    c: Coincident(g29,g2)
    c: Coincident(g29,g14)
    c: Horizontal(g29)
    c: Coincident(g30,g3)
    c: Coincident(g30,g15)
    c: Horizontal(g30)
    c: Coincident(g31,g3)
    c: Coincident(g31,g15)
    c: Horizontal(g31)
    c: Coincident(g32,g4)
    c: Coincident(g32,g16)
    c: Horizontal(g32)
    c: Coincident(g33,g4)
    c: Coincident(g33,g16)
    c: Horizontal(g33)
    c: Coincident(g34,g5)
    c: Coincident(g34,g17)
    c: Horizontal(g34)
    c: Coincident(g35,g5)
    c: Coincident(g35,g17)
    c: Horizontal(g35)
    c: Coincident(g36,g6)
    c: Coincident(g36,g19)
    c: Horizontal(g36)
    c: Coincident(g37,g6)
    c: Coincident(g37,g19)
    c: Horizontal(g37)
    c: Coincident(g38,g7)
    c: Coincident(g38,g18)
    c: Horizontal(g38)
    c: Coincident(g39,g7)
    c: Coincident(g39,g18)
    c: Horizontal(g39)
    c: Coincident(g40,g8)
    c: Coincident(g40,g20)
    c: Horizontal(g40)
    c: Coincident(g41,g8)
    c: Coincident(g41,g20)
    c: Horizontal(g41)
    c: Coincident(g42,g9)
    c: Coincident(g42,g23)
    c: Horizontal(g42)
    c: Coincident(g43,g9)
    c: Coincident(g43,g23)
    c: Horizontal(g43)
    c: Coincident(g44,g10)
    c: Coincident(g44,g22)
    c: Horizontal(g44)
    c: Coincident(g45,g10)
    c: Coincident(g45,g22)
    c: Horizontal(g45)
    c: Coincident(g46,g11)
    c: Coincident(g46,g21)
    c: Horizontal(g46)
    c: Coincident(g47,g11)
    c: Coincident(g47,g21)
    c: Horizontal(g47)
FEATURE [Part::Extrusion] Extrude023
  Base = -> Sketch032
  Dir = (1,-2e-16,2e-16)
  DirMode = 2
  FaceMakerClass = Part::FaceMakerBullseye
  LengthFwd = 19
  LengthRev = 0
  Placement = pos=(-19,0,0) rot=(0,0,1;0rad)
  Solid = true
  Symmetric = false
FEATURE [Part::Fillet] Fillet023
  Base = -> Extrude023
  Edges = 24 edges r=1.49: [Edge6,Edge11,Edge18,Edge23,Edge30,Edge35,Edge42,Edge47,Edge54,Edge59,Edge66,Edge71,Edge78,Edge83,Edge90,Edge95,Edge102,Edge107,Edge114,Edge119,Edge126,Edge131,Edge138,Edge143]
  Placement = pos=(0,0.05,0) rot=(0,0,1;0rad)
FEATURE [Part::Cut] Cut014  label="bottom003"
  Base = -> Cut007
  Tool = -> Fusion047
FEATURE [Part::Cut] Cut021  label="bottom004"
  Base = -> Cut014
  Tool = -> Fillet023
FEATURE [Sketcher::SketchObject] Sketch033
  FullyConstrained = true
  Placement = pos=(117,19,0) rot=(0.57735,0.57735,0.57735;2.0944rad)
  sketch-geometry (8):
    g0: LineSegment StartX=-49.19 StartY=69.25 StartZ=0 EndX=-49.19 EndY=66.25 EndZ=0
    g1: LineSegment StartX=-49.19 StartY=5.75 StartZ=0 EndX=-49.19 EndY=2.75 EndZ=0
    g2: ArcOfCircle CenterX=-1.5 CenterY=67.75 CenterZ=0 NormalX=0 NormalY=0 NormalZ=1 AngleXU=0 Radius=1.5 StartAngle=4.71239 EndAngle=7.85398
    g3: ArcOfCircle CenterX=-1.5 CenterY=4.25 CenterZ=0 NormalX=0 NormalY=0 NormalZ=1 AngleXU=0 Radius=1.5 StartAngle=4.71239 EndAngle=7.85398
    g4: LineSegment StartX=-49.19 StartY=69.25 StartZ=0 EndX=-1.5 EndY=69.25 EndZ=0
    g5: LineSegment StartX=-49.19 StartY=66.25 StartZ=0 EndX=-1.5 EndY=66.25 EndZ=0
    g6: LineSegment StartX=-49.19 StartY=5.75 StartZ=0 EndX=-1.5 EndY=5.75 EndZ=0
    g7: LineSegment StartX=-49.19 StartY=2.75 StartZ=0 EndX=-1.5 EndY=2.75 EndZ=0
  constraints (19):
    c: Vertical(g0)
    c: Distance(g0) = 3
    c: Block(g0)
    c: Vertical(g1)
    c: Block(g2)
    c: Block(g3)
    c: Block(g1)
    c: Coincident(g4,g0)
    c: Coincident(g4,g2)
    c: Horizontal(g4)
    c: Coincident(g5,g0)
    c: Coincident(g5,g2)
    c: Horizontal(g5)
    c: Coincident(g6,g1)
    c: Coincident(g6,g3)
    c: Horizontal(g6)
    c: Coincident(g7,g1)
    c: Coincident(g7,g3)
    c: Horizontal(g7)
FEATURE [Sketcher::SketchObject] Sketch034
  FullyConstrained = true
  Placement = pos=(117,19,0) rot=(0.57735,0.57735,0.57735;2.0944rad)
  sketch-geometry (8):
    g0: LineSegment StartX=-49.19 StartY=63.5 StartZ=0 EndX=-49.19 EndY=60.5 EndZ=0
    g1: LineSegment StartX=-49.19 StartY=11.5 StartZ=0 EndX=-49.19 EndY=8.5 EndZ=0
    g2: ArcOfCircle CenterX=-1.5 CenterY=62 CenterZ=0 NormalX=0 NormalY=0 NormalZ=1 AngleXU=0 Radius=1.5 StartAngle=4.71239 EndAngle=7.85398
    g3: ArcOfCircle CenterX=-1.5 CenterY=10 CenterZ=0 NormalX=0 NormalY=0 NormalZ=1 AngleXU=0 Radius=1.5 StartAngle=4.71239 EndAngle=7.85398
    g4: LineSegment StartX=-49.19 StartY=63.5 StartZ=0 EndX=-1.5 EndY=63.5 EndZ=0
    g5: LineSegment StartX=-49.19 StartY=60.5 StartZ=0 EndX=-1.5 EndY=60.5 EndZ=0
    g6: LineSegment StartX=-49.19 StartY=11.5 StartZ=0 EndX=-1.5 EndY=11.5 EndZ=0
    g7: LineSegment StartX=-49.19 StartY=8.5 StartZ=0 EndX=-1.5 EndY=8.5 EndZ=0
  constraints (19):
    c: Vertical(g0)
    c: Distance(g0) = 3
    c: Vertical(g1)
    c: Block(g1)
    c: Block(g2)
    c: Block(g3)
    c: Block(g0)
    c: Coincident(g4,g0)
    c: Coincident(g4,g2)
    c: Horizontal(g4)
    c: Coincident(g5,g0)
    c: Coincident(g5,g2)
    c: Horizontal(g5)
    c: Coincident(g6,g1)
    c: Coincident(g6,g3)
    c: Horizontal(g6)
    c: Coincident(g7,g1)
    c: Coincident(g7,g3)
    c: Horizontal(g7)
FEATURE [Part::Extrusion] Extrude024
  Base = -> Sketch033
  Dir = (1,0,0)
  DirMode = 2
  FaceMakerClass = Part::FaceMakerBullseye
  LengthFwd = 10
  LengthRev = 0
  Solid = true
  Symmetric = false
FEATURE [Part::Extrusion] Extrude025
  Base = -> Sketch034
  Dir = (1,0,0)
  DirMode = 2
  FaceMakerClass = Part::FaceMakerBullseye
  LengthFwd = 10
  LengthRev = 0
  Solid = true
  Symmetric = false
FEATURE [Part::Fillet] Fillet024  label="removeFromtMoreFrontCaseScrewRetainers"
  Base = -> Extrude024
  Edges = 4 edges r=1.49: [Edge6,Edge11,Edge18,Edge23]
  Placement = pos=(-11,0,0) rot=(0,0,1;0rad)
FEATURE [Part::Fillet] Fillet025  label="removeFromtMoreFrontCaseScrewRetainers001"
  Base = -> Extrude025
  Edges = 4 edges r=1.49: [Edge6,Edge11,Edge18,Edge23]
  Placement = pos=(-19,0,0) rot=(0,0,1;0rad)
FEATURE [Part::Cut] Cut022
  Base = -> Cut015
  Tool = -> Fillet025
FEATURE [Part::Cut] Cut023  label="screwRetainers"
  Base = -> Cut022
  Tool = -> Fillet024
FEATURE [Part::MultiFuse] Fusion056  label="bottom005"
  Shapes = -> [Fusion044,Cut021]
FEATURE [Part::MultiFuse] Fusion057  label="casePillars001"
  Shapes = -> [Cut016,Fusion052]
FEATURE [Part::MultiFuse] Fusion058  label="bottom006"
  Shapes = -> [Fusion056,Cut023]
FEATURE [Part::MultiFuse] Fusion059  label="bottom007"
  Shapes = -> [Fusion058,Fillet005]
FEATURE [Part::MultiFuse] Fusion060  label="bottom008"
  Shapes = -> [Fusion059,Fusion]
FEATURE [Part::MultiFuse] Fusion061  label="top011"
  Shapes = -> [Cut006,Cut020]
FEATURE [Part::MultiFuse] Fusion062  label="top012"
  Shapes = -> [Fusion057,Fusion061]
FEATURE [Part::MultiFuse] Fusion063  label="top013"
  Shapes = -> [Fusion062,Extrude003,Extrude002]
FEATURE [Sketcher::SketchObject] Sketch035  label="topSketch007"
  FullyConstrained = true
  sketch-geometry (6):
    g0: LineSegment StartX=19 StartY=38 StartZ=0 EndX=117 EndY=38 EndZ=0
    g1: ArcOfCircle CenterX=19 CenterY=19 CenterZ=0 NormalX=0 NormalY=0 NormalZ=1 AngleXU=0 Radius=19 StartAngle=1.5708 EndAngle=3.14159
    g2: LineSegment StartX=117 StartY=38 StartZ=0 EndX=117 EndY=19 EndZ=0
    g3: LineSegment StartX=98 StartY=1.0161e-12 StartZ=0 EndX=5.22862e-06 EndY=1.0161e-12 EndZ=0
    g4: LineSegment StartX=5.22862e-06 StartY=19 StartZ=0 EndX=5.22862e-06 EndY=1.0161e-12 EndZ=0
    g5: ArcOfCircle CenterX=98 CenterY=19 CenterZ=0 NormalX=0 NormalY=0 NormalZ=1 AngleXU=0 Radius=19 StartAngle=4.71239 EndAngle=6.28319
  constraints (16):
    c: Horizontal(g0)
    c: Distance(g0) = 98
    c: Coincident(g1,g0)
    c: Block(g1)
    c: Coincident(g2,g0)
    c: Vertical(g2)
    c: Distance(g2) = 19
    c: Horizontal(g3)
    c: Coincident(g4,g1)
    c: Vertical(g4)
    c: Coincident(g3,g4)
    c: Block(g3)
    c: Coincident(g5,g2)
    c: Coincident(g5,g3)
    c: Block(g0)
    c: Block(g5)
FEATURE [Part::Extrusion] Extrude026  label="sideA001"
  Base = -> Sketch035
  Dir = (0,0,1)
  DirMode = 2
  FaceMakerClass = Part::FaceMakerBullseye
  LengthFwd = 3
  LengthRev = 0
  Placement = pos=(0,0,-2.7) rot=(0,0,1;0rad)
  Solid = true
  Symmetric = false
FEATURE [Sketcher::SketchObject] Sketch036  label="topSketch008"
  FullyConstrained = true
  sketch-geometry (6):
    g0: LineSegment StartX=19 StartY=38 StartZ=0 EndX=117 EndY=38 EndZ=0
    g1: ArcOfCircle CenterX=19 CenterY=19 CenterZ=0 NormalX=0 NormalY=0 NormalZ=1 AngleXU=0 Radius=19 StartAngle=1.5708 EndAngle=3.14159
    g2: LineSegment StartX=117 StartY=38 StartZ=0 EndX=117 EndY=19 EndZ=0
    g3: LineSegment StartX=98 StartY=1.0161e-12 StartZ=0 EndX=5.22862e-06 EndY=1.0161e-12 EndZ=0
    g4: LineSegment StartX=5.22862e-06 StartY=19 StartZ=0 EndX=5.22862e-06 EndY=1.0161e-12 EndZ=0
    g5: ArcOfCircle CenterX=98 CenterY=19 CenterZ=0 NormalX=0 NormalY=0 NormalZ=1 AngleXU=0 Radius=19 StartAngle=4.71239 EndAngle=6.28319
  constraints (16):
    c: Horizontal(g0)
    c: Distance(g0) = 98
    c: Coincident(g1,g0)
    c: Block(g1)
    c: Coincident(g2,g0)
    c: Vertical(g2)
    c: Distance(g2) = 19
    c: Horizontal(g3)
    c: Coincident(g4,g1)
    c: Vertical(g4)
    c: Coincident(g3,g4)
    c: Block(g3)
    c: Coincident(g5,g2)
    c: Coincident(g5,g3)
    c: Block(g0)
    c: Block(g5)
FEATURE [Part::Extrusion] Extrude027  label="sideB001"
  Base = -> Sketch036
  Dir = (0,0,1)
  DirMode = 2
  FaceMakerClass = Part::FaceMakerBullseye
  LengthFwd = 3
  LengthRev = 0
  Placement = pos=(0,0,71.7) rot=(0,0,1;0rad)
  Solid = true
  Symmetric = false
FEATURE [Part::MultiFuse] Fusion064  label="removeFromBottom"
  Shapes = -> [Extrude026,Extrude027]
FEATURE [Part::Cut] Cut024  label="bottom009"
  Base = -> Fusion060
  Tool = -> Fusion064
